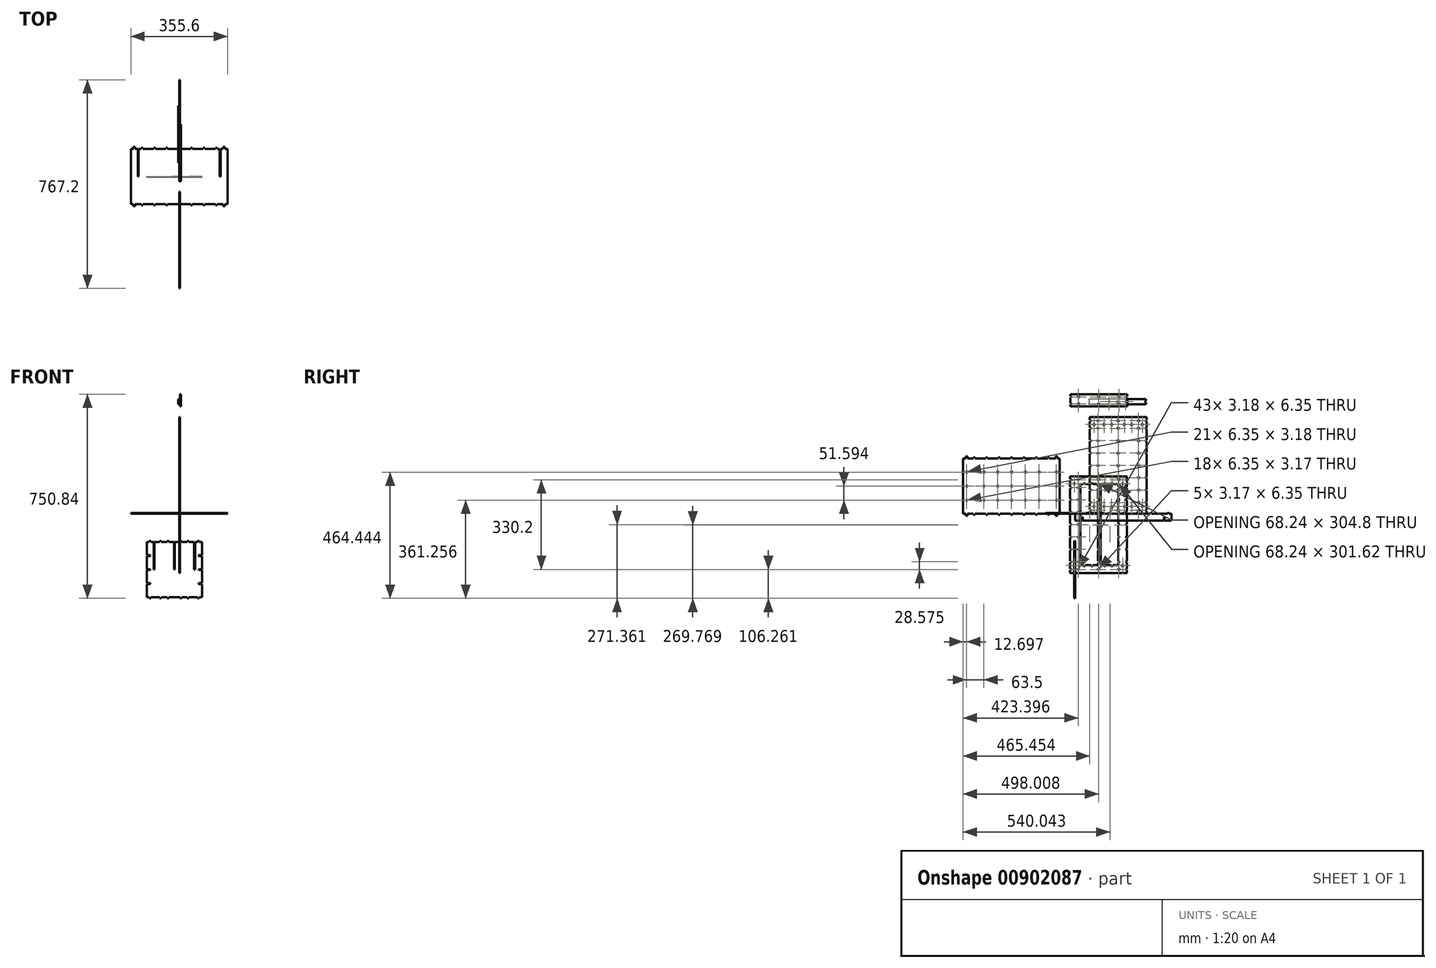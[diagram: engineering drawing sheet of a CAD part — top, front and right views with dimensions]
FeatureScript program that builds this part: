
annotation { "Feature Type Name" : "Feature", "Feature Type Description" : "" }
export const myFeature = defineFeature(function(context is Context, id is Id, definition is map)
    precondition{}
    {
        {
            var Q0;
            Q0=qCreatedBy(makeId("Top.planeOp"),FACE);
            var sketch = newSketch(context, id + "F0", { "sketchPlane" : qUnion([Q0])});
            skLineSegment(sketch, "E0.left", {"start": v(-177.8, 101.6) * mm, "end": v(-177.8, -101.6) * mm});
            skLineSegment(sketch, "E0.right", {"start": v(177.8, 101.6) * mm, "end": v(177.8, -101.6) * mm});
            skPoint(sketch, "E0.middle", {"position": v(0, 0) * mm});
            skLineSegment(sketch, "E1", {"start": v(-152.4, 101.6) * mm, "end": v(-152.4, 0) * mm});
            skLineSegment(sketch, "E2", {"start": v(-149.22, 101.6) * mm, "end": v(-149.22, 0) * mm});
            skLineSegment(sketch, "E3", {"start": v(-152.4, 0) * mm, "end": v(-149.22, 0) * mm});
            skLineSegment(sketch, "E4", {"start": v(149.22, 101.6) * mm, "end": v(149.22, 0) * mm});
            skLineSegment(sketch, "E5", {"start": v(152.4, 101.6) * mm, "end": v(152.4, 0) * mm});
            skLineSegment(sketch, "E6", {"start": v(152.4, 0) * mm, "end": v(149.22, 0) * mm});
            skLineSegment(sketch, "E7", {"start": v(177.8, 101.6) * mm, "end": v(168.28, 101.6) * mm});
            skLineSegment(sketch, "E8", {"start": v(168.28, 101.6) * mm, "end": v(168.28, 105.57) * mm});
            skLineSegment(sketch, "E9", {"start": v(161.93, 105.57) * mm, "end": v(161.93, 101.6) * mm});
            skLineSegment(sketch, "E10", {"start": v(161.93, 101.6) * mm, "end": v(152.4, 101.6) * mm});
            skLineSegment(sketch, "E11", {"start": v(-152.4, 101.6) * mm, "end": v(-161.92, 101.6) * mm});
            skLineSegment(sketch, "E12", {"start": v(-161.92, 101.6) * mm, "end": v(-161.92, 105.57) * mm});
            skLineSegment(sketch, "E13", {"start": v(-168.27, 105.57) * mm, "end": v(-168.27, 101.6) * mm});
            skLineSegment(sketch, "E14", {"start": v(-168.27, 101.6) * mm, "end": v(-177.8, 101.6) * mm});
            skLineSegment(sketch, "E15", {"start": v(-133.35, 101.6) * mm, "end": v(-133.35, 105.57) * mm});
            skLineSegment(sketch, "E16", {"start": v(-133.35, 105.57) * mm, "end": v(-139.7, 105.57) * mm});
            skLineSegment(sketch, "E17", {"start": v(-139.7, 105.57) * mm, "end": v(-139.7, 101.6) * mm});
            skLineSegment(sketch, "E18", {"start": v(48.68, 101.6) * mm, "end": v(48.68, 105.57) * mm});
            skLineSegment(sketch, "E19", {"start": v(48.68, 105.57) * mm, "end": v(42.33, 105.57) * mm});
            skLineSegment(sketch, "E20", {"start": v(42.33, 105.57) * mm, "end": v(42.33, 101.6) * mm});
            skLineSegment(sketch, "E21", {"start": v(-42.33, 101.6) * mm, "end": v(-42.33, 105.57) * mm});
            skLineSegment(sketch, "E22", {"start": v(-42.33, 105.57) * mm, "end": v(-48.68, 105.57) * mm});
            skLineSegment(sketch, "E23", {"start": v(-48.68, 105.57) * mm, "end": v(-48.68, 101.6) * mm});
            skLineSegment(sketch, "E24", {"start": v(3.18, 101.6) * mm, "end": v(3.18, 105.57) * mm});
            skLineSegment(sketch, "E25", {"start": v(3.18, 105.57) * mm, "end": v(-3.17, 105.57) * mm});
            skLineSegment(sketch, "E26", {"start": v(-3.17, 105.57) * mm, "end": v(-3.17, 101.6) * mm});
            skLineSegment(sketch, "E27", {"start": v(139.7, 101.6) * mm, "end": v(139.7, 105.57) * mm});
            skLineSegment(sketch, "E28", {"start": v(139.7, 105.57) * mm, "end": v(133.35, 105.57) * mm});
            skLineSegment(sketch, "E29", {"start": v(133.35, 105.57) * mm, "end": v(133.35, 101.6) * mm});
            skLineSegment(sketch, "E30", {"start": v(149.22, 101.6) * mm, "end": v(139.7, 101.6) * mm});
            skLineSegment(sketch, "E31", {"start": v(42.33, 101.6) * mm, "end": v(3.18, 101.6) * mm});
            skLineSegment(sketch, "E32", {"start": v(-3.17, 101.6) * mm, "end": v(-42.33, 101.6) * mm});
            skLineSegment(sketch, "E33", {"start": v(-139.7, 101.6) * mm, "end": v(-149.22, 101.6) * mm});
            skLineSegment(sketch, "E34", {"start": v(94.2, 101.6) * mm, "end": v(94.2, 105.57) * mm});
            skLineSegment(sketch, "E35", {"start": v(94.2, 105.57) * mm, "end": v(87.84, 105.57) * mm});
            skLineSegment(sketch, "E36", {"start": v(87.84, 105.57) * mm, "end": v(87.84, 101.6) * mm});
            skLineSegment(sketch, "E37", {"start": v(-87.84, 101.6) * mm, "end": v(-87.84, 105.57) * mm});
            skLineSegment(sketch, "E38", {"start": v(-87.84, 105.57) * mm, "end": v(-94.2, 105.57) * mm});
            skLineSegment(sketch, "E39", {"start": v(-94.2, 105.57) * mm, "end": v(-94.2, 101.6) * mm});
            skLineSegment(sketch, "E40", {"start": v(-48.68, 101.6) * mm, "end": v(-87.84, 101.6) * mm});
            skLineSegment(sketch, "E41", {"start": v(-94.2, 101.6) * mm, "end": v(-133.35, 101.6) * mm});
            skLineSegment(sketch, "E42", {"start": v(133.35, 101.6) * mm, "end": v(94.2, 101.6) * mm});
            skLineSegment(sketch, "E43", {"start": v(87.84, 101.6) * mm, "end": v(48.68, 101.6) * mm});
            skLineSegment(sketch, "E44", {"start": v(-177.8, -101.6) * mm, "end": v(-168.27, -101.6) * mm});
            skLineSegment(sketch, "E45", {"start": v(-168.27, -101.6) * mm, "end": v(-168.27, -105.57) * mm});
            skLineSegment(sketch, "E46", {"start": v(-161.92, -105.57) * mm, "end": v(-161.92, -101.6) * mm});
            skLineSegment(sketch, "E47", {"start": v(-161.92, -101.6) * mm, "end": v(-152.4, -101.6) * mm});
            skLineSegment(sketch, "E48", {"start": v(152.4, -101.6) * mm, "end": v(161.93, -101.6) * mm});
            skLineSegment(sketch, "E49", {"start": v(161.93, -101.6) * mm, "end": v(161.93, -105.57) * mm});
            skLineSegment(sketch, "E50", {"start": v(168.28, -105.57) * mm, "end": v(168.28, -101.6) * mm});
            skLineSegment(sketch, "E51", {"start": v(168.28, -101.6) * mm, "end": v(177.8, -101.6) * mm});
            skLineSegment(sketch, "E52", {"start": v(133.35, -101.6) * mm, "end": v(133.35, -105.57) * mm});
            skLineSegment(sketch, "E53", {"start": v(133.35, -105.57) * mm, "end": v(139.7, -105.57) * mm});
            skLineSegment(sketch, "E54", {"start": v(139.7, -105.57) * mm, "end": v(139.7, -101.6) * mm});
            skLineSegment(sketch, "E55", {"start": v(-48.68, -101.6) * mm, "end": v(-48.68, -105.57) * mm});
            skLineSegment(sketch, "E56", {"start": v(-48.68, -105.57) * mm, "end": v(-42.33, -105.57) * mm});
            skLineSegment(sketch, "E57", {"start": v(-42.33, -105.57) * mm, "end": v(-42.33, -101.6) * mm});
            skLineSegment(sketch, "E58", {"start": v(42.33, -101.6) * mm, "end": v(42.33, -105.57) * mm});
            skLineSegment(sketch, "E59", {"start": v(42.33, -105.57) * mm, "end": v(48.68, -105.57) * mm});
            skLineSegment(sketch, "E60", {"start": v(48.68, -105.57) * mm, "end": v(48.68, -101.6) * mm});
            skLineSegment(sketch, "E61", {"start": v(-3.17, -101.6) * mm, "end": v(-3.17, -105.57) * mm});
            skLineSegment(sketch, "E62", {"start": v(-3.17, -105.57) * mm, "end": v(3.18, -105.57) * mm});
            skLineSegment(sketch, "E63", {"start": v(3.18, -105.57) * mm, "end": v(3.18, -101.6) * mm});
            skLineSegment(sketch, "E64", {"start": v(-139.7, -101.6) * mm, "end": v(-139.7, -105.57) * mm});
            skLineSegment(sketch, "E65", {"start": v(-139.7, -105.57) * mm, "end": v(-133.35, -105.57) * mm});
            skLineSegment(sketch, "E66", {"start": v(-133.35, -105.57) * mm, "end": v(-133.35, -101.6) * mm});
            skLineSegment(sketch, "E67", {"start": v(-149.22, -101.6) * mm, "end": v(-139.7, -101.6) * mm});
            skLineSegment(sketch, "E68", {"start": v(-42.33, -101.6) * mm, "end": v(-3.17, -101.6) * mm});
            skLineSegment(sketch, "E69", {"start": v(3.18, -101.6) * mm, "end": v(42.33, -101.6) * mm});
            skLineSegment(sketch, "E70", {"start": v(139.7, -101.6) * mm, "end": v(149.23, -101.6) * mm});
            skLineSegment(sketch, "E71", {"start": v(-94.2, -101.6) * mm, "end": v(-94.2, -105.57) * mm});
            skLineSegment(sketch, "E72", {"start": v(-94.2, -105.57) * mm, "end": v(-87.84, -105.57) * mm});
            skLineSegment(sketch, "E73", {"start": v(-87.84, -105.57) * mm, "end": v(-87.84, -101.6) * mm});
            skLineSegment(sketch, "E74", {"start": v(87.84, -101.6) * mm, "end": v(87.84, -105.57) * mm});
            skLineSegment(sketch, "E75", {"start": v(87.84, -105.57) * mm, "end": v(94.2, -105.57) * mm});
            skLineSegment(sketch, "E76", {"start": v(94.2, -105.57) * mm, "end": v(94.2, -101.6) * mm});
            skLineSegment(sketch, "E77", {"start": v(48.68, -101.6) * mm, "end": v(87.84, -101.6) * mm});
            skLineSegment(sketch, "E78", {"start": v(94.2, -101.6) * mm, "end": v(133.35, -101.6) * mm});
            skLineSegment(sketch, "E79", {"start": v(-133.35, -101.6) * mm, "end": v(-94.2, -101.6) * mm});
            skLineSegment(sketch, "E80", {"start": v(-87.84, -101.6) * mm, "end": v(-48.68, -101.6) * mm});
            skLineSegment(sketch, "E81", {"start": v(152.4, -101.6) * mm, "end": v(149.23, -101.6) * mm});
            skLineSegment(sketch, "E82", {"start": v(-152.4, -101.6) * mm, "end": v(-149.22, -101.6) * mm});
            skLineSegment(sketch, "E83", {"start": v(168.27, 108.87) * mm, "end": v(161.92, 108.87) * mm});
            skLineSegment(sketch, "E84", {"start": v(168.27, 108.87) * mm, "end": v(168.28, 105.57) * mm});
            skLineSegment(sketch, "E85", {"start": v(161.92, 108.87) * mm, "end": v(161.92, 105.57) * mm});
            skLineSegment(sketch, "E86", {"start": v(-161.92, 108.87) * mm, "end": v(-168.27, 108.87) * mm});
            skLineSegment(sketch, "E87", {"start": v(-168.27, 108.87) * mm, "end": v(-168.27, 105.57) * mm});
            skLineSegment(sketch, "E88", {"start": v(-161.92, 105.57) * mm, "end": v(-161.92, 108.87) * mm});
            skLineSegment(sketch, "E89", {"start": v(-168.27, -108.87) * mm, "end": v(-161.92, -108.87) * mm});
            skLineSegment(sketch, "E90", {"start": v(-168.27, -105.57) * mm, "end": v(-168.27, -108.87) * mm});
            skLineSegment(sketch, "E91", {"start": v(-161.92, -105.57) * mm, "end": v(-161.92, -108.87) * mm});
            skLineSegment(sketch, "E92", {"start": v(161.93, -108.87) * mm, "end": v(168.28, -108.87) * mm});
            skLineSegment(sketch, "E93", {"start": v(161.93, -105.57) * mm, "end": v(161.93, -108.87) * mm});
            skLineSegment(sketch, "E94", {"start": v(168.28, -105.57) * mm, "end": v(168.28, -108.87) * mm});
            skSolve(sketch);
        }
        {
            var Q0;
            Q0=makeQuery(id+"F0.imprint","IMPRINT",FACE,{"disambiguationData":[TD([[makeQuery(id+"F0.imprint","IMPRINT",EDGE,{"derivedFrom":sQuery(id+"F0.wireOp",EDGE,"E0.left")}),1.0]])]});
            extrude(context, id + "F1", {"entities" : qUnion([Q0]), "depth" : 3.17 * mm, "offsetDistance" : 25.4 * mm});
        }
        {
            var Q0;
            Q0=qCreatedBy(makeId("Front.planeOp"),FACE);
            var sketch = newSketch(context, id + "F2", { "sketchPlane" : qUnion([Q0])});
            skPoint(sketch, "E95.middle", {"position": v(-17.67, -205.68) * mm});
            skLineSegment(sketch, "E96", {"start": v(-93.87, -104.08) * mm, "end": v(-93.87, -205.68) * mm});
            skLineSegment(sketch, "E97", {"start": v(-90.7, -104.08) * mm, "end": v(-90.7, -205.68) * mm});
            skLineSegment(sketch, "E98", {"start": v(-93.87, -205.68) * mm, "end": v(-90.7, -205.68) * mm});
            skLineSegment(sketch, "E99", {"start": v(55.36, -104.08) * mm, "end": v(55.36, -205.68) * mm});
            skLineSegment(sketch, "E100", {"start": v(58.53, -104.08) * mm, "end": v(58.53, -205.68) * mm});
            skLineSegment(sketch, "E101", {"start": v(58.53, -205.68) * mm, "end": v(55.36, -205.68) * mm});
            skLineSegment(sketch, "E102", {"start": v(-19.25, -205.68) * mm, "end": v(-16.08, -205.68) * mm});
            skLineSegment(sketch, "E103", {"start": v(-119.27, -152.5) * mm, "end": v(-106.57, -152.5) * mm});
            skLineSegment(sketch, "E104", {"start": v(-106.57, -152.5) * mm, "end": v(-106.57, -155.67) * mm});
            skLineSegment(sketch, "E105", {"start": v(-106.57, -155.67) * mm, "end": v(-119.27, -155.67) * mm});
            skLineSegment(sketch, "E106", {"start": v(-119.27, -255.69) * mm, "end": v(-106.57, -255.69) * mm});
            skLineSegment(sketch, "E107", {"start": v(-106.57, -255.69) * mm, "end": v(-106.57, -258.86) * mm});
            skLineSegment(sketch, "E108", {"start": v(-106.57, -258.86) * mm, "end": v(-119.27, -258.86) * mm});
            skLineSegment(sketch, "E109.right", {"start": v(-44.65, -104.08) * mm, "end": v(-44.65, -100.11) * mm});
            skLineSegment(sketch, "E110.bottom", {"start": v(-44.65, -100.11) * mm, "end": v(-38.3, -100.11) * mm});
            skLineSegment(sketch, "E111.right", {"start": v(-38.3, -104.08) * mm, "end": v(-38.3, -100.11) * mm});
            skLineSegment(sketch, "E112.right", {"start": v(-71.64, -104.08) * mm, "end": v(-71.64, -100.11) * mm});
            skLineSegment(sketch, "E113.bottom", {"start": v(-71.64, -100.11) * mm, "end": v(-65.3, -100.11) * mm});
            skLineSegment(sketch, "E114.right", {"start": v(-65.3, -104.08) * mm, "end": v(-65.3, -100.11) * mm});
            skLineSegment(sketch, "E115", {"start": v(-90.7, -104.08) * mm, "end": v(-71.64, -104.08) * mm});
            skLineSegment(sketch, "E116", {"start": v(-65.3, -104.08) * mm, "end": v(-44.65, -104.08) * mm});
            skLineSegment(sketch, "E117", {"start": v(-38.3, -104.08) * mm, "end": v(-19.25, -104.08) * mm});
            skLineSegment(sketch, "E118", {"start": v(-119.27, -104.08) * mm, "end": v(-119.27, -152.5) * mm});
            skLineSegment(sketch, "E119", {"start": v(-119.27, -258.86) * mm, "end": v(-119.27, -307.28) * mm});
            skLineSegment(sketch, "E120", {"start": v(-119.27, -204.1) * mm, "end": v(-106.57, -204.1) * mm});
            skLineSegment(sketch, "E121", {"start": v(-106.57, -204.1) * mm, "end": v(-106.57, -207.27) * mm});
            skLineSegment(sketch, "E122", {"start": v(-106.57, -207.27) * mm, "end": v(-119.27, -207.27) * mm});
            skLineSegment(sketch, "E123", {"start": v(-119.27, -255.69) * mm, "end": v(-119.27, -207.27) * mm});
            skLineSegment(sketch, "E124", {"start": v(-119.27, -204.1) * mm, "end": v(-119.27, -155.67) * mm});
            skLineSegment(sketch, "E125", {"start": v(71.23, -259.78) * mm, "end": v(71.23, -256.6) * mm});
            skLineSegment(sketch, "E126.right", {"start": v(29.96, -104.08) * mm, "end": v(29.96, -100.11) * mm});
            skLineSegment(sketch, "E127.bottom", {"start": v(29.96, -100.11) * mm, "end": v(36.3, -100.11) * mm});
            skLineSegment(sketch, "E128.right", {"start": v(36.3, -104.08) * mm, "end": v(36.3, -100.11) * mm});
            skLineSegment(sketch, "E129.right", {"start": v(2.97, -104.08) * mm, "end": v(2.97, -100.11) * mm});
            skLineSegment(sketch, "E130.bottom", {"start": v(2.97, -100.11) * mm, "end": v(9.32, -100.11) * mm});
            skLineSegment(sketch, "E131.right", {"start": v(9.32, -104.08) * mm, "end": v(9.32, -100.11) * mm});
            skLineSegment(sketch, "E132", {"start": v(-16.08, -104.08) * mm, "end": v(2.97, -104.08) * mm});
            skLineSegment(sketch, "E133", {"start": v(9.32, -104.08) * mm, "end": v(29.96, -104.08) * mm});
            skLineSegment(sketch, "E134", {"start": v(36.3, -104.08) * mm, "end": v(55.36, -104.08) * mm});
            skLineSegment(sketch, "E135.left", {"start": v(74.4, -307.28) * mm, "end": v(74.4, -311.25) * mm});
            skLineSegment(sketch, "E136.right", {"start": v(68.06, -307.28) * mm, "end": v(68.06, -311.25) * mm});
            skLineSegment(sketch, "E137", {"start": v(68.06, -307.28) * mm, "end": v(58.53, -307.28) * mm});
            skLineSegment(sketch, "E138.right", {"start": v(9.32, -307.28) * mm, "end": v(9.32, -311.25) * mm});
            skLineSegment(sketch, "E139.bottom", {"start": v(9.32, -311.25) * mm, "end": v(2.97, -311.25) * mm});
            skLineSegment(sketch, "E140.right", {"start": v(2.97, -307.28) * mm, "end": v(2.97, -311.25) * mm});
            skLineSegment(sketch, "E141.right", {"start": v(36.3, -307.28) * mm, "end": v(36.3, -311.25) * mm});
            skLineSegment(sketch, "E142.bottom", {"start": v(36.3, -311.25) * mm, "end": v(29.96, -311.25) * mm});
            skLineSegment(sketch, "E143.right", {"start": v(29.96, -307.28) * mm, "end": v(29.96, -311.25) * mm});
            skLineSegment(sketch, "E144", {"start": v(55.36, -307.28) * mm, "end": v(36.3, -307.28) * mm});
            skLineSegment(sketch, "E145", {"start": v(29.96, -307.28) * mm, "end": v(9.32, -307.28) * mm});
            skLineSegment(sketch, "E146", {"start": v(2.97, -307.28) * mm, "end": v(-16.08, -307.28) * mm});
            skLineSegment(sketch, "E147.right", {"start": v(-65.3, -307.28) * mm, "end": v(-65.3, -311.25) * mm});
            skLineSegment(sketch, "E148.bottom", {"start": v(-65.3, -311.25) * mm, "end": v(-71.64, -311.25) * mm});
            skLineSegment(sketch, "E149.right", {"start": v(-71.64, -307.28) * mm, "end": v(-71.64, -311.25) * mm});
            skLineSegment(sketch, "E150.right", {"start": v(-38.3, -307.28) * mm, "end": v(-38.3, -311.25) * mm});
            skLineSegment(sketch, "E151.bottom", {"start": v(-38.3, -311.25) * mm, "end": v(-44.65, -311.25) * mm});
            skLineSegment(sketch, "E152.right", {"start": v(-44.65, -307.28) * mm, "end": v(-44.65, -311.25) * mm});
            skLineSegment(sketch, "E153", {"start": v(-19.25, -307.28) * mm, "end": v(-38.3, -307.28) * mm});
            skLineSegment(sketch, "E154", {"start": v(-44.65, -307.28) * mm, "end": v(-65.3, -307.28) * mm});
            skLineSegment(sketch, "E155", {"start": v(-71.64, -307.28) * mm, "end": v(-90.7, -307.28) * mm});
            skLineSegment(sketch, "E156", {"start": v(-93.87, -307.28) * mm, "end": v(-90.7, -307.28) * mm});
            skLineSegment(sketch, "E157", {"start": v(-19.25, -307.28) * mm, "end": v(-16.08, -307.28) * mm});
            skLineSegment(sketch, "E158", {"start": v(55.36, -307.28) * mm, "end": v(58.53, -307.28) * mm});
            skLineSegment(sketch, "E159", {"start": v(83.93, -258.86) * mm, "end": v(71.23, -258.86) * mm});
            skLineSegment(sketch, "E160", {"start": v(71.23, -258.86) * mm, "end": v(71.23, -255.69) * mm});
            skLineSegment(sketch, "E161", {"start": v(71.23, -255.69) * mm, "end": v(83.93, -255.69) * mm});
            skLineSegment(sketch, "E162", {"start": v(83.93, -155.67) * mm, "end": v(71.23, -155.67) * mm});
            skLineSegment(sketch, "E163", {"start": v(71.23, -155.67) * mm, "end": v(71.23, -152.5) * mm});
            skLineSegment(sketch, "E164", {"start": v(71.23, -152.5) * mm, "end": v(83.93, -152.5) * mm});
            skLineSegment(sketch, "E165", {"start": v(83.93, -307.28) * mm, "end": v(83.93, -258.86) * mm});
            skLineSegment(sketch, "E166", {"start": v(83.93, -152.5) * mm, "end": v(83.93, -104.08) * mm});
            skLineSegment(sketch, "E167", {"start": v(83.93, -207.27) * mm, "end": v(71.23, -207.27) * mm});
            skLineSegment(sketch, "E168", {"start": v(71.23, -207.27) * mm, "end": v(71.23, -204.1) * mm});
            skLineSegment(sketch, "E169", {"start": v(71.23, -204.1) * mm, "end": v(83.93, -204.1) * mm});
            skLineSegment(sketch, "E170", {"start": v(83.93, -155.67) * mm, "end": v(83.93, -204.1) * mm});
            skLineSegment(sketch, "E171", {"start": v(83.93, -207.27) * mm, "end": v(83.93, -255.69) * mm});
            skLineSegment(sketch, "E172", {"start": v(74.4, -311.25) * mm, "end": v(68.06, -311.25) * mm});
            skLineSegment(sketch, "E173", {"start": v(83.93, -307.28) * mm, "end": v(74.4, -307.28) * mm});
            skLineSegment(sketch, "E174.left", {"start": v(-103.4, -307.28) * mm, "end": v(-103.4, -311.25) * mm});
            skLineSegment(sketch, "E175.right", {"start": v(-109.74, -307.28) * mm, "end": v(-109.74, -311.25) * mm});
            skLineSegment(sketch, "E176", {"start": v(-109.74, -307.28) * mm, "end": v(-119.27, -307.28) * mm});
            skLineSegment(sketch, "E177", {"start": v(-103.4, -311.25) * mm, "end": v(-109.74, -311.25) * mm});
            skLineSegment(sketch, "E178", {"start": v(-93.87, -307.28) * mm, "end": v(-103.4, -307.28) * mm});
            skLineSegment(sketch, "E179.left", {"start": v(-109.74, -104.08) * mm, "end": v(-109.74, -100.11) * mm});
            skLineSegment(sketch, "E180.right", {"start": v(-103.4, -104.08) * mm, "end": v(-103.4, -100.11) * mm});
            skLineSegment(sketch, "E181", {"start": v(-103.4, -104.08) * mm, "end": v(-93.87, -104.08) * mm});
            skLineSegment(sketch, "E182", {"start": v(-109.74, -100.11) * mm, "end": v(-103.4, -100.11) * mm});
            skLineSegment(sketch, "E183", {"start": v(-119.27, -104.08) * mm, "end": v(-109.74, -104.08) * mm});
            skLineSegment(sketch, "E184.left", {"start": v(68.06, -104.08) * mm, "end": v(68.06, -100.11) * mm});
            skLineSegment(sketch, "E185.right", {"start": v(74.4, -104.08) * mm, "end": v(74.4, -100.11) * mm});
            skLineSegment(sketch, "E186", {"start": v(74.4, -104.08) * mm, "end": v(83.93, -104.08) * mm});
            skLineSegment(sketch, "E187", {"start": v(68.06, -100.11) * mm, "end": v(74.4, -100.11) * mm});
            skLineSegment(sketch, "E188", {"start": v(58.53, -104.08) * mm, "end": v(68.06, -104.08) * mm});
            skLineSegment(sketch, "E189", {"start": v(-19.25, -205.68) * mm, "end": v(-19.25, -104.08) * mm});
            skLineSegment(sketch, "E190", {"start": v(-16.08, -104.08) * mm, "end": v(-16.08, -205.68) * mm});
            skSolve(sketch);
        }
        {
            var Q0;
            Q0=makeQuery(id+"F2.imprint","IMPRINT",FACE,{"disambiguationData":[TD([[makeQuery(id+"F2.imprint","IMPRINT",EDGE,{"derivedFrom":sQuery(id+"F2.wireOp",EDGE,"E96")}),-1.0]])]});
            extrude(context, id + "F3", {"entities" : qUnion([Q0]), "depth" : 3.17 * mm, "offsetDistance" : 25.4 * mm});
        }
        {
            var Q0;
            Q0=qCreatedBy(makeId("Right.planeOp"),FACE);
            var sketch = newSketch(context, id + "F4", { "sketchPlane" : qUnion([Q0])});
            skLineSegment(sketch, "E191.left", {"start": v(0, 0) * mm, "end": v(0, -25.4) * mm});
            skLineSegment(sketch, "E191.right", {"start": v(355.6, 0) * mm, "end": v(355.6, -25.4) * mm});
            skLineSegment(sketch, "E192", {"start": v(28.57, -25.4) * mm, "end": v(28.57, -12.47) * mm});
            skLineSegment(sketch, "E193", {"start": v(25.4, -12.47) * mm, "end": v(28.57, -12.47) * mm});
            skLineSegment(sketch, "E194", {"start": v(25.4, -12.47) * mm, "end": v(25.4, -25.4) * mm});
            skLineSegment(sketch, "E195", {"start": v(330.2, -25.4) * mm, "end": v(330.2, -12.47) * mm});
            skLineSegment(sketch, "E196", {"start": v(327.03, -12.47) * mm, "end": v(330.2, -12.47) * mm});
            skLineSegment(sketch, "E197", {"start": v(327.03, -12.47) * mm, "end": v(327.03, -25.4) * mm});
            skLineSegment(sketch, "E198", {"start": v(355.6, -25.4) * mm, "end": v(330.2, -25.4) * mm});
            skLineSegment(sketch, "E199", {"start": v(327.03, -25.4) * mm, "end": v(28.57, -25.4) * mm});
            skLineSegment(sketch, "E200", {"start": v(25.4, -25.4) * mm, "end": v(0, -25.4) * mm});
            skLineSegment(sketch, "E201.top", {"start": v(9.53, 3.18) * mm, "end": v(15.88, 3.18) * mm});
            skLineSegment(sketch, "E201.left", {"start": v(9.53, 0) * mm, "end": v(9.53, 3.18) * mm});
            skLineSegment(sketch, "E201.right", {"start": v(15.88, 0) * mm, "end": v(15.88, 3.18) * mm});
            skLineSegment(sketch, "E202.top", {"start": v(73.03, 3.18) * mm, "end": v(79.38, 3.18) * mm});
            skLineSegment(sketch, "E202.left", {"start": v(73.03, 0) * mm, "end": v(73.03, 3.18) * mm});
            skLineSegment(sketch, "E202.right", {"start": v(79.38, 0) * mm, "end": v(79.38, 3.18) * mm});
            skLineSegment(sketch, "E203.top", {"start": v(123.83, 3.18) * mm, "end": v(130.18, 3.18) * mm});
            skLineSegment(sketch, "E203.left", {"start": v(123.83, 0) * mm, "end": v(123.83, 3.18) * mm});
            skLineSegment(sketch, "E203.right", {"start": v(130.18, 0) * mm, "end": v(130.18, 3.18) * mm});
            skLineSegment(sketch, "E204.top", {"start": v(174.63, 3.18) * mm, "end": v(180.98, 3.18) * mm});
            skLineSegment(sketch, "E204.left", {"start": v(174.63, 0) * mm, "end": v(174.63, 3.18) * mm});
            skLineSegment(sketch, "E204.right", {"start": v(180.98, 0) * mm, "end": v(180.98, 3.18) * mm});
            skLineSegment(sketch, "E205.top", {"start": v(225.43, 3.18) * mm, "end": v(231.78, 3.18) * mm});
            skLineSegment(sketch, "E205.left", {"start": v(225.43, 0) * mm, "end": v(225.43, 3.18) * mm});
            skLineSegment(sketch, "E205.right", {"start": v(231.78, 0) * mm, "end": v(231.78, 3.18) * mm});
            skLineSegment(sketch, "E206.top", {"start": v(276.23, 3.18) * mm, "end": v(282.58, 3.18) * mm});
            skLineSegment(sketch, "E206.left", {"start": v(276.23, 0) * mm, "end": v(276.23, 3.18) * mm});
            skLineSegment(sketch, "E206.right", {"start": v(282.58, 0) * mm, "end": v(282.58, 3.18) * mm});
            skLineSegment(sketch, "E207.top", {"start": v(339.73, 3.18) * mm, "end": v(346.08, 3.18) * mm});
            skLineSegment(sketch, "E207.left", {"start": v(339.73, 0) * mm, "end": v(339.73, 3.18) * mm});
            skLineSegment(sketch, "E207.right", {"start": v(346.08, 0) * mm, "end": v(346.08, 3.18) * mm});
            skLineSegment(sketch, "E208", {"start": v(355.6, 0) * mm, "end": v(346.08, 0) * mm});
            skLineSegment(sketch, "E209", {"start": v(339.73, 0) * mm, "end": v(282.58, 0) * mm});
            skLineSegment(sketch, "E210", {"start": v(276.23, 0) * mm, "end": v(231.78, 0) * mm});
            skLineSegment(sketch, "E211", {"start": v(225.43, 0) * mm, "end": v(180.98, 0) * mm});
            skLineSegment(sketch, "E212", {"start": v(174.63, 0) * mm, "end": v(130.18, 0) * mm});
            skLineSegment(sketch, "E213", {"start": v(123.83, 0) * mm, "end": v(79.38, 0) * mm});
            skLineSegment(sketch, "E214", {"start": v(73.03, 0) * mm, "end": v(15.88, 0) * mm});
            skLineSegment(sketch, "E215", {"start": v(9.53, 0) * mm, "end": v(0, 0) * mm});
            skSolve(sketch);
        }
        {
            var Q0;
            Q0=makeQuery(id+"F4.imprint","IMPRINT",FACE,{"disambiguationData":[TD([[makeQuery(id+"F4.imprint","IMPRINT",EDGE,{"derivedFrom":sQuery(id+"F4.wireOp",EDGE,"E191.left")}),1.0]])]});
            extrude(context, id + "F5", {"entities" : qUnion([Q0]), "depth" : 3.17 * mm, "offsetDistance" : 25.4 * mm});
        }
        {
            var Q0;
            Q0=qCreatedBy(makeId("Right.planeOp"),FACE);
            var sketch = newSketch(context, id + "F6", { "sketchPlane" : qUnion([Q0])});
            skLineSegment(sketch, "E216.left", {"start": v(-411.6, 203.2) * mm, "end": v(-411.6, 0) * mm});
            skLineSegment(sketch, "E216.right", {"start": v(-56, 203.2) * mm, "end": v(-56, 0) * mm});
            skPoint(sketch, "E216.middle", {"position": v(-233.8, 101.6) * mm});
            skLineSegment(sketch, "E217", {"start": v(-56, 203.2) * mm, "end": v(-65.53, 203.2) * mm});
            skLineSegment(sketch, "E218", {"start": v(-65.53, 203.2) * mm, "end": v(-65.53, 207.17) * mm});
            skLineSegment(sketch, "E219", {"start": v(-71.88, 207.17) * mm, "end": v(-71.88, 203.2) * mm});
            skLineSegment(sketch, "E220", {"start": v(-71.88, 203.2) * mm, "end": v(-81.4, 203.2) * mm});
            skLineSegment(sketch, "E221", {"start": v(-386.2, 203.2) * mm, "end": v(-395.73, 203.2) * mm});
            skLineSegment(sketch, "E222", {"start": v(-395.73, 203.2) * mm, "end": v(-395.73, 207.17) * mm});
            skLineSegment(sketch, "E223", {"start": v(-402.08, 207.17) * mm, "end": v(-402.08, 203.2) * mm});
            skLineSegment(sketch, "E224", {"start": v(-402.08, 203.2) * mm, "end": v(-411.6, 203.2) * mm});
            skLineSegment(sketch, "E225", {"start": v(-367.15, 203.2) * mm, "end": v(-367.15, 207.17) * mm});
            skLineSegment(sketch, "E226", {"start": v(-367.15, 207.17) * mm, "end": v(-373.5, 207.17) * mm});
            skLineSegment(sketch, "E227", {"start": v(-373.5, 207.17) * mm, "end": v(-373.5, 203.2) * mm});
            skLineSegment(sketch, "E228", {"start": v(-185.12, 203.2) * mm, "end": v(-185.12, 207.17) * mm});
            skLineSegment(sketch, "E229", {"start": v(-185.12, 207.17) * mm, "end": v(-191.47, 207.17) * mm});
            skLineSegment(sketch, "E230", {"start": v(-191.47, 207.17) * mm, "end": v(-191.47, 203.2) * mm});
            skLineSegment(sketch, "E231", {"start": v(-276.14, 203.2) * mm, "end": v(-276.14, 207.17) * mm});
            skLineSegment(sketch, "E232", {"start": v(-276.14, 207.17) * mm, "end": v(-282.49, 207.17) * mm});
            skLineSegment(sketch, "E233", {"start": v(-282.49, 207.17) * mm, "end": v(-282.49, 203.2) * mm});
            skLineSegment(sketch, "E234", {"start": v(-230.63, 203.2) * mm, "end": v(-230.63, 207.17) * mm});
            skLineSegment(sketch, "E235", {"start": v(-230.63, 207.17) * mm, "end": v(-236.98, 207.17) * mm});
            skLineSegment(sketch, "E236", {"start": v(-236.98, 207.17) * mm, "end": v(-236.98, 203.2) * mm});
            skLineSegment(sketch, "E237", {"start": v(-94.1, 203.2) * mm, "end": v(-94.1, 207.17) * mm});
            skLineSegment(sketch, "E238", {"start": v(-94.1, 207.17) * mm, "end": v(-100.45, 207.17) * mm});
            skLineSegment(sketch, "E239", {"start": v(-100.45, 207.17) * mm, "end": v(-100.45, 203.2) * mm});
            skLineSegment(sketch, "E240", {"start": v(-84.58, 203.2) * mm, "end": v(-94.1, 203.2) * mm});
            skLineSegment(sketch, "E241", {"start": v(-191.47, 203.2) * mm, "end": v(-230.63, 203.2) * mm});
            skLineSegment(sketch, "E242", {"start": v(-236.98, 203.2) * mm, "end": v(-276.14, 203.2) * mm});
            skLineSegment(sketch, "E243", {"start": v(-373.5, 203.2) * mm, "end": v(-383.03, 203.2) * mm});
            skLineSegment(sketch, "E244", {"start": v(-139.61, 203.2) * mm, "end": v(-139.61, 207.17) * mm});
            skLineSegment(sketch, "E245", {"start": v(-139.61, 207.17) * mm, "end": v(-145.96, 207.17) * mm});
            skLineSegment(sketch, "E246", {"start": v(-145.96, 207.17) * mm, "end": v(-145.96, 203.2) * mm});
            skLineSegment(sketch, "E247", {"start": v(-321.65, 203.2) * mm, "end": v(-321.65, 207.17) * mm});
            skLineSegment(sketch, "E248", {"start": v(-321.65, 207.17) * mm, "end": v(-328, 207.17) * mm});
            skLineSegment(sketch, "E249", {"start": v(-328, 207.17) * mm, "end": v(-328, 203.2) * mm});
            skLineSegment(sketch, "E250", {"start": v(-282.49, 203.2) * mm, "end": v(-321.65, 203.2) * mm});
            skLineSegment(sketch, "E251", {"start": v(-328, 203.2) * mm, "end": v(-367.15, 203.2) * mm});
            skLineSegment(sketch, "E252", {"start": v(-100.45, 203.2) * mm, "end": v(-139.61, 203.2) * mm});
            skLineSegment(sketch, "E253", {"start": v(-145.96, 203.2) * mm, "end": v(-185.12, 203.2) * mm});
            skLineSegment(sketch, "E254", {"start": v(-411.6, 0) * mm, "end": v(-402.08, 0) * mm});
            skLineSegment(sketch, "E255", {"start": v(-402.08, 0) * mm, "end": v(-402.08, -3.97) * mm});
            skLineSegment(sketch, "E256", {"start": v(-395.73, -3.97) * mm, "end": v(-395.73, 0) * mm});
            skLineSegment(sketch, "E257", {"start": v(-395.73, 0) * mm, "end": v(-386.2, 0) * mm});
            skLineSegment(sketch, "E258", {"start": v(-81.4, 0) * mm, "end": v(-71.88, 0) * mm});
            skLineSegment(sketch, "E259", {"start": v(-71.88, 0) * mm, "end": v(-71.88, -3.97) * mm});
            skLineSegment(sketch, "E260", {"start": v(-65.53, -3.97) * mm, "end": v(-65.53, 0) * mm});
            skLineSegment(sketch, "E261", {"start": v(-65.53, 0) * mm, "end": v(-56, 0) * mm});
            skLineSegment(sketch, "E262", {"start": v(-100.45, 0) * mm, "end": v(-100.45, -3.97) * mm});
            skLineSegment(sketch, "E263", {"start": v(-100.45, -3.97) * mm, "end": v(-94.1, -3.97) * mm});
            skLineSegment(sketch, "E264", {"start": v(-94.1, -3.97) * mm, "end": v(-94.1, 0) * mm});
            skLineSegment(sketch, "E265", {"start": v(-282.49, 0) * mm, "end": v(-282.49, -3.97) * mm});
            skLineSegment(sketch, "E266", {"start": v(-282.49, -3.97) * mm, "end": v(-276.14, -3.97) * mm});
            skLineSegment(sketch, "E267", {"start": v(-276.14, -3.97) * mm, "end": v(-276.14, 0) * mm});
            skLineSegment(sketch, "E268", {"start": v(-191.47, 0) * mm, "end": v(-191.47, -3.97) * mm});
            skLineSegment(sketch, "E269", {"start": v(-191.47, -3.97) * mm, "end": v(-185.12, -3.97) * mm});
            skLineSegment(sketch, "E270", {"start": v(-185.12, -3.97) * mm, "end": v(-185.12, 0) * mm});
            skLineSegment(sketch, "E271", {"start": v(-236.98, 0) * mm, "end": v(-236.98, -3.97) * mm});
            skLineSegment(sketch, "E272", {"start": v(-236.98, -3.97) * mm, "end": v(-230.63, -3.97) * mm});
            skLineSegment(sketch, "E273", {"start": v(-230.63, -3.97) * mm, "end": v(-230.63, 0) * mm});
            skLineSegment(sketch, "E274", {"start": v(-373.5, 0) * mm, "end": v(-373.5, -3.97) * mm});
            skLineSegment(sketch, "E275", {"start": v(-373.5, -3.97) * mm, "end": v(-367.15, -3.97) * mm});
            skLineSegment(sketch, "E276", {"start": v(-367.15, -3.97) * mm, "end": v(-367.15, 0) * mm});
            skLineSegment(sketch, "E277", {"start": v(-383.03, 0) * mm, "end": v(-373.5, 0) * mm});
            skLineSegment(sketch, "E278", {"start": v(-276.14, 0) * mm, "end": v(-236.98, 0) * mm});
            skLineSegment(sketch, "E279", {"start": v(-230.63, 0) * mm, "end": v(-191.47, 0) * mm});
            skLineSegment(sketch, "E280", {"start": v(-94.1, 0) * mm, "end": v(-84.58, 0) * mm});
            skLineSegment(sketch, "E281", {"start": v(-328, 0) * mm, "end": v(-328, -3.97) * mm});
            skLineSegment(sketch, "E282", {"start": v(-328, -3.97) * mm, "end": v(-321.65, -3.97) * mm});
            skLineSegment(sketch, "E283", {"start": v(-321.65, -3.97) * mm, "end": v(-321.65, 0) * mm});
            skLineSegment(sketch, "E284", {"start": v(-145.96, 0) * mm, "end": v(-145.96, -3.97) * mm});
            skLineSegment(sketch, "E285", {"start": v(-145.96, -3.97) * mm, "end": v(-139.61, -3.97) * mm});
            skLineSegment(sketch, "E286", {"start": v(-139.61, -3.97) * mm, "end": v(-139.61, 0) * mm});
            skLineSegment(sketch, "E287", {"start": v(-185.12, 0) * mm, "end": v(-145.96, 0) * mm});
            skLineSegment(sketch, "E288", {"start": v(-139.61, 0) * mm, "end": v(-100.45, 0) * mm});
            skLineSegment(sketch, "E289", {"start": v(-367.15, 0) * mm, "end": v(-328, 0) * mm});
            skLineSegment(sketch, "E290", {"start": v(-321.65, 0) * mm, "end": v(-282.49, 0) * mm});
            skLineSegment(sketch, "E291", {"start": v(-81.4, 0) * mm, "end": v(-84.58, 0) * mm});
            skLineSegment(sketch, "E292", {"start": v(-386.2, 0) * mm, "end": v(-383.03, 0) * mm});
            skLineSegment(sketch, "E293", {"start": v(-81.4, 203.2) * mm, "end": v(-84.58, 203.2) * mm});
            skLineSegment(sketch, "E294", {"start": v(-386.2, 203.2) * mm, "end": v(-383.03, 203.2) * mm});
            skLineSegment(sketch, "E295.bottom", {"start": v(-65.53, 154.78) * mm, "end": v(-71.88, 154.78) * mm});
            skLineSegment(sketch, "E295.top", {"start": v(-65.53, 151.6) * mm, "end": v(-71.88, 151.6) * mm});
            skLineSegment(sketch, "E295.left", {"start": v(-65.53, 154.78) * mm, "end": v(-65.53, 151.6) * mm});
            skLineSegment(sketch, "E295.right", {"start": v(-71.88, 154.78) * mm, "end": v(-71.88, 151.6) * mm});
            skLineSegment(sketch, "E296.bottom", {"start": v(-129.03, 154.78) * mm, "end": v(-135.38, 154.78) * mm});
            skLineSegment(sketch, "E296.top", {"start": v(-129.03, 151.6) * mm, "end": v(-135.38, 151.6) * mm});
            skLineSegment(sketch, "E296.left", {"start": v(-129.03, 154.78) * mm, "end": v(-129.03, 151.6) * mm});
            skLineSegment(sketch, "E296.right", {"start": v(-135.38, 154.78) * mm, "end": v(-135.38, 151.6) * mm});
            skLineSegment(sketch, "E297.bottom", {"start": v(-179.83, 154.78) * mm, "end": v(-186.18, 154.78) * mm});
            skLineSegment(sketch, "E297.top", {"start": v(-179.83, 151.6) * mm, "end": v(-186.18, 151.6) * mm});
            skLineSegment(sketch, "E297.left", {"start": v(-179.83, 154.78) * mm, "end": v(-179.83, 151.6) * mm});
            skLineSegment(sketch, "E297.right", {"start": v(-186.18, 154.78) * mm, "end": v(-186.18, 151.6) * mm});
            skLineSegment(sketch, "E298.bottom", {"start": v(-230.63, 154.78) * mm, "end": v(-236.98, 154.78) * mm});
            skLineSegment(sketch, "E298.top", {"start": v(-230.63, 151.6) * mm, "end": v(-236.98, 151.6) * mm});
            skLineSegment(sketch, "E298.left", {"start": v(-230.63, 154.78) * mm, "end": v(-230.63, 151.6) * mm});
            skLineSegment(sketch, "E298.right", {"start": v(-236.98, 154.78) * mm, "end": v(-236.98, 151.6) * mm});
            skLineSegment(sketch, "E299.bottom", {"start": v(-281.43, 154.78) * mm, "end": v(-287.78, 154.78) * mm});
            skLineSegment(sketch, "E299.top", {"start": v(-281.43, 151.6) * mm, "end": v(-287.78, 151.6) * mm});
            skLineSegment(sketch, "E299.left", {"start": v(-281.43, 154.78) * mm, "end": v(-281.43, 151.6) * mm});
            skLineSegment(sketch, "E299.right", {"start": v(-287.78, 154.78) * mm, "end": v(-287.78, 151.6) * mm});
            skLineSegment(sketch, "E300.bottom", {"start": v(-332.23, 154.78) * mm, "end": v(-338.58, 154.78) * mm});
            skLineSegment(sketch, "E300.top", {"start": v(-332.23, 151.6) * mm, "end": v(-338.58, 151.6) * mm});
            skLineSegment(sketch, "E300.left", {"start": v(-332.23, 154.78) * mm, "end": v(-332.23, 151.6) * mm});
            skLineSegment(sketch, "E300.right", {"start": v(-338.58, 154.78) * mm, "end": v(-338.58, 151.6) * mm});
            skLineSegment(sketch, "E301.bottom", {"start": v(-395.73, 154.78) * mm, "end": v(-402.08, 154.78) * mm});
            skLineSegment(sketch, "E301.top", {"start": v(-395.73, 151.6) * mm, "end": v(-402.08, 151.6) * mm});
            skLineSegment(sketch, "E301.left", {"start": v(-395.73, 154.78) * mm, "end": v(-395.73, 151.6) * mm});
            skLineSegment(sketch, "E301.right", {"start": v(-402.08, 154.78) * mm, "end": v(-402.08, 151.6) * mm});
            skLineSegment(sketch, "E302.bottom", {"start": v(-65.53, 103.19) * mm, "end": v(-71.88, 103.19) * mm});
            skLineSegment(sketch, "E302.top", {"start": v(-65.53, 100.01) * mm, "end": v(-71.88, 100.01) * mm});
            skLineSegment(sketch, "E302.left", {"start": v(-65.53, 103.19) * mm, "end": v(-65.53, 100.01) * mm});
            skLineSegment(sketch, "E302.right", {"start": v(-71.88, 103.19) * mm, "end": v(-71.88, 100.01) * mm});
            skLineSegment(sketch, "E303.bottom", {"start": v(-129.03, 103.19) * mm, "end": v(-135.38, 103.19) * mm});
            skLineSegment(sketch, "E303.top", {"start": v(-129.03, 100.01) * mm, "end": v(-135.38, 100.01) * mm});
            skLineSegment(sketch, "E303.left", {"start": v(-129.03, 103.19) * mm, "end": v(-129.03, 100.01) * mm});
            skLineSegment(sketch, "E303.right", {"start": v(-135.38, 103.19) * mm, "end": v(-135.38, 100.01) * mm});
            skLineSegment(sketch, "E304.bottom", {"start": v(-179.83, 103.19) * mm, "end": v(-186.18, 103.19) * mm});
            skLineSegment(sketch, "E304.top", {"start": v(-179.83, 100.01) * mm, "end": v(-186.18, 100.01) * mm});
            skLineSegment(sketch, "E304.left", {"start": v(-179.83, 103.19) * mm, "end": v(-179.83, 100.01) * mm});
            skLineSegment(sketch, "E304.right", {"start": v(-186.18, 103.19) * mm, "end": v(-186.18, 100.01) * mm});
            skLineSegment(sketch, "E305.bottom", {"start": v(-230.63, 103.19) * mm, "end": v(-236.98, 103.19) * mm});
            skLineSegment(sketch, "E305.top", {"start": v(-230.63, 100.01) * mm, "end": v(-236.98, 100.01) * mm});
            skLineSegment(sketch, "E305.left", {"start": v(-230.63, 103.19) * mm, "end": v(-230.63, 100.01) * mm});
            skLineSegment(sketch, "E305.right", {"start": v(-236.98, 103.19) * mm, "end": v(-236.98, 100.01) * mm});
            skLineSegment(sketch, "E306.bottom", {"start": v(-281.43, 103.19) * mm, "end": v(-287.78, 103.19) * mm});
            skLineSegment(sketch, "E306.top", {"start": v(-281.43, 100.01) * mm, "end": v(-287.78, 100.01) * mm});
            skLineSegment(sketch, "E306.left", {"start": v(-281.43, 103.19) * mm, "end": v(-281.43, 100.01) * mm});
            skLineSegment(sketch, "E306.right", {"start": v(-287.78, 103.19) * mm, "end": v(-287.78, 100.01) * mm});
            skLineSegment(sketch, "E307.bottom", {"start": v(-332.23, 103.19) * mm, "end": v(-338.58, 103.19) * mm});
            skLineSegment(sketch, "E307.top", {"start": v(-332.23, 100.01) * mm, "end": v(-338.58, 100.01) * mm});
            skLineSegment(sketch, "E307.left", {"start": v(-332.23, 103.19) * mm, "end": v(-332.23, 100.01) * mm});
            skLineSegment(sketch, "E307.right", {"start": v(-338.58, 103.19) * mm, "end": v(-338.58, 100.01) * mm});
            skLineSegment(sketch, "E308.bottom", {"start": v(-395.73, 103.19) * mm, "end": v(-402.08, 103.19) * mm});
            skLineSegment(sketch, "E308.top", {"start": v(-395.73, 100.01) * mm, "end": v(-402.08, 100.01) * mm});
            skLineSegment(sketch, "E308.left", {"start": v(-395.73, 103.19) * mm, "end": v(-395.73, 100.01) * mm});
            skLineSegment(sketch, "E308.right", {"start": v(-402.08, 103.19) * mm, "end": v(-402.08, 100.01) * mm});
            skLineSegment(sketch, "E309.bottom", {"start": v(-65.53, 51.6) * mm, "end": v(-71.88, 51.6) * mm});
            skLineSegment(sketch, "E309.top", {"start": v(-65.53, 48.42) * mm, "end": v(-71.88, 48.42) * mm});
            skLineSegment(sketch, "E309.left", {"start": v(-65.53, 51.6) * mm, "end": v(-65.53, 48.42) * mm});
            skLineSegment(sketch, "E309.right", {"start": v(-71.88, 51.6) * mm, "end": v(-71.88, 48.42) * mm});
            skLineSegment(sketch, "E310.bottom", {"start": v(-129.03, 51.6) * mm, "end": v(-135.38, 51.6) * mm});
            skLineSegment(sketch, "E310.top", {"start": v(-129.03, 48.42) * mm, "end": v(-135.38, 48.42) * mm});
            skLineSegment(sketch, "E310.left", {"start": v(-129.03, 51.6) * mm, "end": v(-129.03, 48.42) * mm});
            skLineSegment(sketch, "E310.right", {"start": v(-135.38, 51.6) * mm, "end": v(-135.38, 48.42) * mm});
            skLineSegment(sketch, "E311.bottom", {"start": v(-179.83, 51.6) * mm, "end": v(-186.18, 51.6) * mm});
            skLineSegment(sketch, "E311.top", {"start": v(-179.83, 48.42) * mm, "end": v(-186.18, 48.42) * mm});
            skLineSegment(sketch, "E311.left", {"start": v(-179.83, 51.6) * mm, "end": v(-179.83, 48.42) * mm});
            skLineSegment(sketch, "E311.right", {"start": v(-186.18, 51.6) * mm, "end": v(-186.18, 48.42) * mm});
            skLineSegment(sketch, "E312.bottom", {"start": v(-230.63, 51.6) * mm, "end": v(-236.98, 51.6) * mm});
            skLineSegment(sketch, "E312.top", {"start": v(-230.63, 48.42) * mm, "end": v(-236.98, 48.42) * mm});
            skLineSegment(sketch, "E312.left", {"start": v(-230.63, 51.6) * mm, "end": v(-230.63, 48.42) * mm});
            skLineSegment(sketch, "E312.right", {"start": v(-236.98, 51.6) * mm, "end": v(-236.98, 48.42) * mm});
            skLineSegment(sketch, "E313.bottom", {"start": v(-281.43, 51.6) * mm, "end": v(-287.78, 51.6) * mm});
            skLineSegment(sketch, "E313.top", {"start": v(-281.43, 48.42) * mm, "end": v(-287.78, 48.42) * mm});
            skLineSegment(sketch, "E313.left", {"start": v(-281.43, 51.6) * mm, "end": v(-281.43, 48.42) * mm});
            skLineSegment(sketch, "E313.right", {"start": v(-287.78, 51.6) * mm, "end": v(-287.78, 48.42) * mm});
            skLineSegment(sketch, "E314.bottom", {"start": v(-332.23, 51.6) * mm, "end": v(-338.58, 51.6) * mm});
            skLineSegment(sketch, "E314.top", {"start": v(-332.23, 48.42) * mm, "end": v(-338.58, 48.42) * mm});
            skLineSegment(sketch, "E314.left", {"start": v(-332.23, 51.6) * mm, "end": v(-332.23, 48.42) * mm});
            skLineSegment(sketch, "E314.right", {"start": v(-338.58, 51.6) * mm, "end": v(-338.58, 48.42) * mm});
            skLineSegment(sketch, "E315.bottom", {"start": v(-395.73, 51.6) * mm, "end": v(-402.08, 51.6) * mm});
            skLineSegment(sketch, "E315.top", {"start": v(-395.73, 48.42) * mm, "end": v(-402.08, 48.42) * mm});
            skLineSegment(sketch, "E315.left", {"start": v(-395.73, 51.6) * mm, "end": v(-395.73, 48.42) * mm});
            skLineSegment(sketch, "E315.right", {"start": v(-402.08, 51.6) * mm, "end": v(-402.08, 48.42) * mm});
            skLineSegment(sketch, "E316", {"start": v(-395.73, 210.46) * mm, "end": v(-402.08, 210.46) * mm});
            skLineSegment(sketch, "E317", {"start": v(-395.73, 207.17) * mm, "end": v(-395.73, 210.46) * mm});
            skLineSegment(sketch, "E318", {"start": v(-402.08, 207.17) * mm, "end": v(-402.08, 210.46) * mm});
            skLineSegment(sketch, "E319", {"start": v(-65.53, 210.46) * mm, "end": v(-71.88, 210.46) * mm});
            skLineSegment(sketch, "E320", {"start": v(-71.88, 207.17) * mm, "end": v(-71.88, 210.46) * mm});
            skLineSegment(sketch, "E321", {"start": v(-65.53, 210.46) * mm, "end": v(-65.53, 207.17) * mm});
            skLineSegment(sketch, "E322", {"start": v(-71.88, -7.27) * mm, "end": v(-65.53, -7.27) * mm});
            skLineSegment(sketch, "E323", {"start": v(-65.53, -7.27) * mm, "end": v(-65.53, -3.97) * mm});
            skLineSegment(sketch, "E324", {"start": v(-71.88, -7.27) * mm, "end": v(-71.88, -3.97) * mm});
            skLineSegment(sketch, "E325", {"start": v(-402.08, -7.27) * mm, "end": v(-395.73, -7.27) * mm});
            skLineSegment(sketch, "E326", {"start": v(-402.08, -7.27) * mm, "end": v(-402.08, -3.97) * mm});
            skLineSegment(sketch, "E327", {"start": v(-395.73, -3.97) * mm, "end": v(-395.73, -7.27) * mm});
            skSolve(sketch);
        }
        {
            var Q0;
            Q0 = qSketchRegion(id + "F6", true);
            extrude(context, id + "F7", {"entities" : qUnion([Q0]), "depth" : 3.17 * mm, "offsetDistance" : 25.4 * mm});
        }
        {
            var Q0;
            Q0=qCreatedBy(makeId("Right.planeOp"),FACE);
            var sketch = newSketch(context, id + "F8", { "sketchPlane" : qUnion([Q0])});
            skLineSegment(sketch, "E328.bottom", {"start": v(54.04, 0) * mm, "end": v(263.6, 0) * mm});
            skLineSegment(sketch, "E328.top", {"start": v(54.04, 355.6) * mm, "end": v(263.6, 355.6) * mm});
            skLineSegment(sketch, "E329.left", {"start": v(66.74, 25.4) * mm, "end": v(66.74, 28.58) * mm});
            skLineSegment(sketch, "E330.right", {"start": v(131.02, 25.4) * mm, "end": v(131.02, 28.58) * mm});
            skLineSegment(sketch, "E331.bottom", {"start": v(131.02, 28.58) * mm, "end": v(137.37, 28.58) * mm});
            skLineSegment(sketch, "E332.right", {"start": v(137.37, 25.4) * mm, "end": v(137.37, 28.58) * mm});
            skLineSegment(sketch, "E333.right", {"start": v(104.04, 25.4) * mm, "end": v(104.04, 28.58) * mm});
            skLineSegment(sketch, "E334.bottom", {"start": v(104.04, 28.58) * mm, "end": v(110.39, 28.58) * mm});
            skLineSegment(sketch, "E335.right", {"start": v(110.39, 25.4) * mm, "end": v(110.39, 28.58) * mm});
            skLineSegment(sketch, "E336.left", {"start": v(244.54, 25.4) * mm, "end": v(244.54, 28.57) * mm});
            skLineSegment(sketch, "E337.top", {"start": v(244.54, 28.57) * mm, "end": v(250.9, 28.57) * mm});
            skLineSegment(sketch, "E338.right", {"start": v(250.9, 25.4) * mm, "end": v(250.9, 28.57) * mm});
            skLineSegment(sketch, "E339.right", {"start": v(205.64, 25.4) * mm, "end": v(205.64, 28.58) * mm});
            skLineSegment(sketch, "E340.bottom", {"start": v(205.64, 28.58) * mm, "end": v(211.99, 28.58) * mm});
            skLineSegment(sketch, "E341.right", {"start": v(211.99, 25.4) * mm, "end": v(211.99, 28.58) * mm});
            skLineSegment(sketch, "E342.right", {"start": v(178.65, 25.4) * mm, "end": v(178.65, 28.57) * mm});
            skLineSegment(sketch, "E343.bottom", {"start": v(178.65, 28.57) * mm, "end": v(185, 28.57) * mm});
            skLineSegment(sketch, "E344.right", {"start": v(185, 25.4) * mm, "end": v(185, 28.57) * mm});
            skLineSegment(sketch, "E345", {"start": v(250.9, 25.4) * mm, "end": v(244.54, 25.4) * mm});
            skLineSegment(sketch, "E346", {"start": v(211.99, 25.4) * mm, "end": v(205.64, 25.4) * mm});
            skLineSegment(sketch, "E347", {"start": v(185, 25.4) * mm, "end": v(178.65, 25.4) * mm});
            skLineSegment(sketch, "E348", {"start": v(137.37, 25.4) * mm, "end": v(131.02, 25.4) * mm});
            skLineSegment(sketch, "E349", {"start": v(110.39, 25.4) * mm, "end": v(104.04, 25.4) * mm});
            skLineSegment(sketch, "E350", {"start": v(73.1, 25.4) * mm, "end": v(66.74, 25.4) * mm});
            skLineSegment(sketch, "E351", {"start": v(66.74, 28.58) * mm, "end": v(73.1, 28.58) * mm});
            skLineSegment(sketch, "E352", {"start": v(73.1, 28.58) * mm, "end": v(73.1, 25.4) * mm});
            skLineSegment(sketch, "E353.left", {"start": v(66.74, 327.03) * mm, "end": v(66.74, 330.2) * mm});
            skLineSegment(sketch, "E354.right", {"start": v(131.02, 327.02) * mm, "end": v(131.02, 330.2) * mm});
            skLineSegment(sketch, "E355.bottom", {"start": v(131.02, 330.2) * mm, "end": v(137.37, 330.2) * mm});
            skLineSegment(sketch, "E356.right", {"start": v(137.37, 327.02) * mm, "end": v(137.37, 330.2) * mm});
            skLineSegment(sketch, "E357.right", {"start": v(104.04, 327.03) * mm, "end": v(104.04, 330.2) * mm});
            skLineSegment(sketch, "E358.bottom", {"start": v(104.04, 330.2) * mm, "end": v(110.39, 330.2) * mm});
            skLineSegment(sketch, "E359.right", {"start": v(110.39, 327.03) * mm, "end": v(110.39, 330.2) * mm});
            skLineSegment(sketch, "E360.left", {"start": v(244.54, 327.02) * mm, "end": v(244.54, 330.2) * mm});
            skLineSegment(sketch, "E361.top", {"start": v(244.54, 330.2) * mm, "end": v(250.9, 330.2) * mm});
            skLineSegment(sketch, "E362.right", {"start": v(250.9, 327.02) * mm, "end": v(250.9, 330.2) * mm});
            skLineSegment(sketch, "E363.right", {"start": v(205.64, 327.02) * mm, "end": v(205.64, 330.2) * mm});
            skLineSegment(sketch, "E364.bottom", {"start": v(205.64, 330.2) * mm, "end": v(211.99, 330.2) * mm});
            skLineSegment(sketch, "E365.right", {"start": v(211.99, 327.02) * mm, "end": v(211.99, 330.2) * mm});
            skLineSegment(sketch, "E366.right", {"start": v(178.65, 327.02) * mm, "end": v(178.65, 330.2) * mm});
            skLineSegment(sketch, "E367.bottom", {"start": v(178.65, 330.2) * mm, "end": v(185, 330.2) * mm});
            skLineSegment(sketch, "E368.right", {"start": v(185, 327.02) * mm, "end": v(185, 330.2) * mm});
            skLineSegment(sketch, "E369", {"start": v(250.9, 327.02) * mm, "end": v(244.54, 327.02) * mm});
            skLineSegment(sketch, "E370", {"start": v(211.99, 327.03) * mm, "end": v(205.64, 327.03) * mm});
            skLineSegment(sketch, "E371", {"start": v(185, 327.02) * mm, "end": v(178.65, 327.02) * mm});
            skLineSegment(sketch, "E372", {"start": v(137.37, 327.03) * mm, "end": v(131.02, 327.03) * mm});
            skLineSegment(sketch, "E373", {"start": v(110.39, 327.02) * mm, "end": v(104.04, 327.02) * mm});
            skLineSegment(sketch, "E374", {"start": v(73.1, 327.02) * mm, "end": v(66.74, 327.02) * mm});
            skLineSegment(sketch, "E375", {"start": v(66.74, 330.2) * mm, "end": v(73.1, 330.2) * mm});
            skLineSegment(sketch, "E376", {"start": v(73.1, 330.2) * mm, "end": v(73.1, 327.02) * mm});
            skLineSegment(sketch, "E377.left", {"start": v(98.5, 25.4) * mm, "end": v(98.5, 28.58) * mm});
            skLineSegment(sketch, "E378", {"start": v(82.62, 9.53) * mm, "end": v(85.8, 9.53) * mm});
            skLineSegment(sketch, "E379", {"start": v(85.8, 9.53) * mm, "end": v(85.8, 15.88) * mm});
            skLineSegment(sketch, "E380", {"start": v(85.8, 15.87) * mm, "end": v(82.62, 15.87) * mm});
            skLineSegment(sketch, "E381", {"start": v(82.62, 339.72) * mm, "end": v(85.8, 339.72) * mm});
            skLineSegment(sketch, "E382", {"start": v(85.8, 339.72) * mm, "end": v(85.8, 346.07) * mm});
            skLineSegment(sketch, "E383", {"start": v(85.8, 346.07) * mm, "end": v(82.62, 346.07) * mm});
            skLineSegment(sketch, "E384", {"start": v(82.62, 311.15) * mm, "end": v(85.8, 311.15) * mm});
            skLineSegment(sketch, "E385", {"start": v(85.8, 311.15) * mm, "end": v(85.8, 317.5) * mm});
            skLineSegment(sketch, "E386", {"start": v(85.8, 317.5) * mm, "end": v(82.62, 317.5) * mm});
            skLineSegment(sketch, "E387", {"start": v(82.62, 129.12) * mm, "end": v(85.8, 129.12) * mm});
            skLineSegment(sketch, "E388", {"start": v(85.8, 129.12) * mm, "end": v(85.8, 135.47) * mm});
            skLineSegment(sketch, "E389", {"start": v(85.8, 135.47) * mm, "end": v(82.62, 135.47) * mm});
            skLineSegment(sketch, "E390", {"start": v(82.62, 220.13) * mm, "end": v(85.8, 220.13) * mm});
            skLineSegment(sketch, "E391", {"start": v(85.8, 220.13) * mm, "end": v(85.8, 226.48) * mm});
            skLineSegment(sketch, "E392", {"start": v(85.8, 226.48) * mm, "end": v(82.62, 226.48) * mm});
            skLineSegment(sketch, "E393", {"start": v(82.62, 174.62) * mm, "end": v(85.8, 174.62) * mm});
            skLineSegment(sketch, "E394", {"start": v(85.8, 174.62) * mm, "end": v(85.8, 180.97) * mm});
            skLineSegment(sketch, "E395", {"start": v(85.8, 180.97) * mm, "end": v(82.62, 180.97) * mm});
            skLineSegment(sketch, "E396", {"start": v(82.62, 38.1) * mm, "end": v(85.8, 38.1) * mm});
            skLineSegment(sketch, "E397", {"start": v(85.8, 38.1) * mm, "end": v(85.8, 44.45) * mm});
            skLineSegment(sketch, "E398", {"start": v(85.8, 44.45) * mm, "end": v(82.62, 44.45) * mm});
            skLineSegment(sketch, "E399", {"start": v(82.62, 83.6) * mm, "end": v(85.8, 83.6) * mm});
            skLineSegment(sketch, "E400", {"start": v(85.8, 83.6) * mm, "end": v(85.8, 89.96) * mm});
            skLineSegment(sketch, "E401", {"start": v(85.8, 89.96) * mm, "end": v(82.62, 89.96) * mm});
            skLineSegment(sketch, "E402", {"start": v(82.62, 265.64) * mm, "end": v(85.8, 265.64) * mm});
            skLineSegment(sketch, "E403", {"start": v(85.8, 265.64) * mm, "end": v(85.8, 272) * mm});
            skLineSegment(sketch, "E404", {"start": v(85.8, 272) * mm, "end": v(82.62, 272) * mm});
            skLineSegment(sketch, "E405.left", {"start": v(228.67, 330.2) * mm, "end": v(228.67, 327.02) * mm});
            skLineSegment(sketch, "E406", {"start": v(54.04, 9.53) * mm, "end": v(57.22, 9.53) * mm});
            skLineSegment(sketch, "E407", {"start": v(57.22, 9.53) * mm, "end": v(57.22, 15.88) * mm});
            skLineSegment(sketch, "E408", {"start": v(57.22, 15.88) * mm, "end": v(54.04, 15.88) * mm});
            skLineSegment(sketch, "E409", {"start": v(54.04, 15.88) * mm, "end": v(54.04, 25.4) * mm});
            skLineSegment(sketch, "E410", {"start": v(54.04, 330.2) * mm, "end": v(54.04, 339.73) * mm});
            skLineSegment(sketch, "E411", {"start": v(54.04, 339.73) * mm, "end": v(57.22, 339.73) * mm});
            skLineSegment(sketch, "E412", {"start": v(57.22, 339.73) * mm, "end": v(57.22, 346.08) * mm});
            skLineSegment(sketch, "E413", {"start": v(57.22, 346.08) * mm, "end": v(54.04, 346.08) * mm});
            skLineSegment(sketch, "E414", {"start": v(54.04, 311.15) * mm, "end": v(57.22, 311.15) * mm});
            skLineSegment(sketch, "E415", {"start": v(57.22, 311.15) * mm, "end": v(57.22, 317.5) * mm});
            skLineSegment(sketch, "E416", {"start": v(57.22, 317.5) * mm, "end": v(54.04, 317.5) * mm});
            skLineSegment(sketch, "E417", {"start": v(54.04, 129.12) * mm, "end": v(57.22, 129.12) * mm});
            skLineSegment(sketch, "E418", {"start": v(57.22, 129.12) * mm, "end": v(57.22, 135.47) * mm});
            skLineSegment(sketch, "E419", {"start": v(57.22, 135.47) * mm, "end": v(54.04, 135.47) * mm});
            skLineSegment(sketch, "E420", {"start": v(54.04, 220.13) * mm, "end": v(57.22, 220.13) * mm});
            skLineSegment(sketch, "E421", {"start": v(57.22, 220.13) * mm, "end": v(57.22, 226.48) * mm});
            skLineSegment(sketch, "E422", {"start": v(57.22, 226.48) * mm, "end": v(54.04, 226.48) * mm});
            skLineSegment(sketch, "E423", {"start": v(54.04, 174.63) * mm, "end": v(57.22, 174.63) * mm});
            skLineSegment(sketch, "E424", {"start": v(57.22, 174.63) * mm, "end": v(57.22, 180.98) * mm});
            skLineSegment(sketch, "E425", {"start": v(57.22, 180.98) * mm, "end": v(54.04, 180.98) * mm});
            skLineSegment(sketch, "E426", {"start": v(54.04, 38.1) * mm, "end": v(57.22, 38.1) * mm});
            skLineSegment(sketch, "E427", {"start": v(57.22, 38.1) * mm, "end": v(57.22, 44.45) * mm});
            skLineSegment(sketch, "E428", {"start": v(57.22, 44.45) * mm, "end": v(54.04, 44.45) * mm});
            skLineSegment(sketch, "E429", {"start": v(54.04, 28.58) * mm, "end": v(54.04, 38.1) * mm});
            skLineSegment(sketch, "E430", {"start": v(54.04, 135.47) * mm, "end": v(54.04, 174.63) * mm});
            skLineSegment(sketch, "E431", {"start": v(54.04, 180.98) * mm, "end": v(54.04, 220.13) * mm});
            skLineSegment(sketch, "E432", {"start": v(54.04, 317.5) * mm, "end": v(54.04, 327.03) * mm});
            skLineSegment(sketch, "E433", {"start": v(54.04, 83.6) * mm, "end": v(57.22, 83.6) * mm});
            skLineSegment(sketch, "E434", {"start": v(57.22, 83.6) * mm, "end": v(57.22, 89.96) * mm});
            skLineSegment(sketch, "E435", {"start": v(57.22, 89.96) * mm, "end": v(54.04, 89.96) * mm});
            skLineSegment(sketch, "E436", {"start": v(54.04, 265.64) * mm, "end": v(57.22, 265.64) * mm});
            skLineSegment(sketch, "E437", {"start": v(57.22, 265.64) * mm, "end": v(57.22, 272) * mm});
            skLineSegment(sketch, "E438", {"start": v(57.22, 272) * mm, "end": v(54.04, 272) * mm});
            skLineSegment(sketch, "E439", {"start": v(54.04, 226.48) * mm, "end": v(54.04, 265.64) * mm});
            skLineSegment(sketch, "E440", {"start": v(54.04, 272) * mm, "end": v(54.04, 311.15) * mm});
            skLineSegment(sketch, "E441", {"start": v(54.04, 44.45) * mm, "end": v(54.04, 83.6) * mm});
            skLineSegment(sketch, "E442", {"start": v(54.04, 89.96) * mm, "end": v(54.04, 129.12) * mm});
            skLineSegment(sketch, "E443", {"start": v(54.04, 330.2) * mm, "end": v(54.04, 327.03) * mm});
            skLineSegment(sketch, "E444", {"start": v(54.04, 25.4) * mm, "end": v(54.04, 28.58) * mm});
            skLineSegment(sketch, "E445", {"start": v(263.6, 346.07) * mm, "end": v(260.42, 346.07) * mm});
            skLineSegment(sketch, "E446", {"start": v(260.42, 346.07) * mm, "end": v(260.42, 339.72) * mm});
            skLineSegment(sketch, "E447", {"start": v(260.42, 339.72) * mm, "end": v(263.6, 339.72) * mm});
            skLineSegment(sketch, "E448", {"start": v(263.6, 339.72) * mm, "end": v(263.6, 330.2) * mm});
            skLineSegment(sketch, "E449", {"start": v(263.6, 25.4) * mm, "end": v(263.6, 15.87) * mm});
            skLineSegment(sketch, "E450", {"start": v(263.6, 15.87) * mm, "end": v(260.42, 15.87) * mm});
            skLineSegment(sketch, "E451", {"start": v(260.42, 15.87) * mm, "end": v(260.42, 9.52) * mm});
            skLineSegment(sketch, "E452", {"start": v(260.42, 9.52) * mm, "end": v(263.6, 9.52) * mm});
            skLineSegment(sketch, "E453", {"start": v(263.6, 44.45) * mm, "end": v(260.42, 44.45) * mm});
            skLineSegment(sketch, "E454", {"start": v(260.42, 44.45) * mm, "end": v(260.42, 38.1) * mm});
            skLineSegment(sketch, "E455", {"start": v(260.42, 38.1) * mm, "end": v(263.6, 38.1) * mm});
            skLineSegment(sketch, "E456", {"start": v(263.6, 226.48) * mm, "end": v(260.42, 226.48) * mm});
            skLineSegment(sketch, "E457", {"start": v(260.42, 226.48) * mm, "end": v(260.42, 220.13) * mm});
            skLineSegment(sketch, "E458", {"start": v(260.42, 220.13) * mm, "end": v(263.6, 220.13) * mm});
            skLineSegment(sketch, "E459", {"start": v(263.6, 135.47) * mm, "end": v(260.42, 135.47) * mm});
            skLineSegment(sketch, "E460", {"start": v(260.42, 135.47) * mm, "end": v(260.42, 129.12) * mm});
            skLineSegment(sketch, "E461", {"start": v(260.42, 129.12) * mm, "end": v(263.6, 129.12) * mm});
            skLineSegment(sketch, "E462", {"start": v(263.6, 180.97) * mm, "end": v(260.42, 180.97) * mm});
            skLineSegment(sketch, "E463", {"start": v(260.42, 180.97) * mm, "end": v(260.42, 174.62) * mm});
            skLineSegment(sketch, "E464", {"start": v(260.42, 174.62) * mm, "end": v(263.6, 174.62) * mm});
            skLineSegment(sketch, "E465", {"start": v(263.6, 317.5) * mm, "end": v(260.42, 317.5) * mm});
            skLineSegment(sketch, "E466", {"start": v(260.42, 317.5) * mm, "end": v(260.42, 311.15) * mm});
            skLineSegment(sketch, "E467", {"start": v(260.42, 311.15) * mm, "end": v(263.6, 311.15) * mm});
            skLineSegment(sketch, "E468", {"start": v(263.6, 327.02) * mm, "end": v(263.6, 317.5) * mm});
            skLineSegment(sketch, "E469", {"start": v(263.6, 220.13) * mm, "end": v(263.6, 180.97) * mm});
            skLineSegment(sketch, "E470", {"start": v(263.6, 174.62) * mm, "end": v(263.6, 135.47) * mm});
            skLineSegment(sketch, "E471", {"start": v(263.6, 38.1) * mm, "end": v(263.6, 28.57) * mm});
            skLineSegment(sketch, "E472", {"start": v(263.6, 272) * mm, "end": v(260.42, 272) * mm});
            skLineSegment(sketch, "E473", {"start": v(260.42, 272) * mm, "end": v(260.42, 265.64) * mm});
            skLineSegment(sketch, "E474", {"start": v(260.42, 265.64) * mm, "end": v(263.6, 265.64) * mm});
            skLineSegment(sketch, "E475", {"start": v(263.6, 89.96) * mm, "end": v(260.42, 89.96) * mm});
            skLineSegment(sketch, "E476", {"start": v(260.42, 89.96) * mm, "end": v(260.42, 83.6) * mm});
            skLineSegment(sketch, "E477", {"start": v(260.42, 83.6) * mm, "end": v(263.6, 83.6) * mm});
            skLineSegment(sketch, "E478", {"start": v(263.6, 129.12) * mm, "end": v(263.6, 89.96) * mm});
            skLineSegment(sketch, "E479", {"start": v(263.6, 265.64) * mm, "end": v(263.6, 226.48) * mm});
            skLineSegment(sketch, "E480", {"start": v(263.6, 25.4) * mm, "end": v(263.6, 28.57) * mm});
            skLineSegment(sketch, "E481", {"start": v(263.6, 330.2) * mm, "end": v(263.6, 327.02) * mm});
            skLineSegment(sketch, "E482", {"start": v(231.84, 9.52) * mm, "end": v(235.02, 9.52) * mm});
            skLineSegment(sketch, "E483", {"start": v(235.02, 9.52) * mm, "end": v(235.02, 15.87) * mm});
            skLineSegment(sketch, "E484", {"start": v(235.02, 15.87) * mm, "end": v(231.84, 15.87) * mm});
            skLineSegment(sketch, "E485", {"start": v(231.84, 339.72) * mm, "end": v(235.02, 339.72) * mm});
            skLineSegment(sketch, "E486", {"start": v(235.02, 339.72) * mm, "end": v(235.02, 346.07) * mm});
            skLineSegment(sketch, "E487", {"start": v(235.02, 346.07) * mm, "end": v(231.84, 346.07) * mm});
            skLineSegment(sketch, "E488", {"start": v(231.84, 311.15) * mm, "end": v(235.02, 311.15) * mm});
            skLineSegment(sketch, "E489", {"start": v(235.02, 311.15) * mm, "end": v(235.02, 317.5) * mm});
            skLineSegment(sketch, "E490", {"start": v(235.02, 317.5) * mm, "end": v(231.84, 317.5) * mm});
            skLineSegment(sketch, "E491", {"start": v(231.84, 129.12) * mm, "end": v(235.02, 129.12) * mm});
            skLineSegment(sketch, "E492", {"start": v(235.02, 129.12) * mm, "end": v(235.02, 135.47) * mm});
            skLineSegment(sketch, "E493", {"start": v(235.02, 135.47) * mm, "end": v(231.84, 135.47) * mm});
            skLineSegment(sketch, "E494", {"start": v(231.84, 220.13) * mm, "end": v(235.02, 220.13) * mm});
            skLineSegment(sketch, "E495", {"start": v(235.02, 220.13) * mm, "end": v(235.02, 226.48) * mm});
            skLineSegment(sketch, "E496", {"start": v(235.02, 226.48) * mm, "end": v(231.84, 226.48) * mm});
            skLineSegment(sketch, "E497", {"start": v(231.84, 174.62) * mm, "end": v(235.02, 174.62) * mm});
            skLineSegment(sketch, "E498", {"start": v(235.02, 174.62) * mm, "end": v(235.02, 180.97) * mm});
            skLineSegment(sketch, "E499", {"start": v(235.02, 180.97) * mm, "end": v(231.84, 180.97) * mm});
            skLineSegment(sketch, "E500", {"start": v(231.84, 38.1) * mm, "end": v(235.02, 38.1) * mm});
            skLineSegment(sketch, "E501", {"start": v(235.02, 38.1) * mm, "end": v(235.02, 44.45) * mm});
            skLineSegment(sketch, "E502", {"start": v(235.02, 44.45) * mm, "end": v(231.84, 44.45) * mm});
            skLineSegment(sketch, "E503", {"start": v(231.84, 83.6) * mm, "end": v(235.02, 83.6) * mm});
            skLineSegment(sketch, "E504", {"start": v(235.02, 83.6) * mm, "end": v(235.02, 89.96) * mm});
            skLineSegment(sketch, "E505", {"start": v(235.02, 89.96) * mm, "end": v(231.84, 89.96) * mm});
            skLineSegment(sketch, "E506", {"start": v(231.84, 265.64) * mm, "end": v(235.02, 265.64) * mm});
            skLineSegment(sketch, "E507", {"start": v(235.02, 265.64) * mm, "end": v(235.02, 272) * mm});
            skLineSegment(sketch, "E508", {"start": v(235.02, 272) * mm, "end": v(231.84, 272) * mm});
            skLineSegment(sketch, "E509", {"start": v(231.84, 330.2) * mm, "end": v(231.84, 327.02) * mm});
            skLineSegment(sketch, "E510", {"start": v(157.23, 9.52) * mm, "end": v(160.4, 9.52) * mm});
            skLineSegment(sketch, "E511", {"start": v(160.4, 9.52) * mm, "end": v(160.4, 15.87) * mm});
            skLineSegment(sketch, "E512", {"start": v(160.4, 15.87) * mm, "end": v(157.23, 15.87) * mm});
            skLineSegment(sketch, "E513", {"start": v(157.23, 339.72) * mm, "end": v(160.4, 339.72) * mm});
            skLineSegment(sketch, "E514", {"start": v(160.4, 339.72) * mm, "end": v(160.4, 346.07) * mm});
            skLineSegment(sketch, "E515", {"start": v(160.4, 346.07) * mm, "end": v(157.23, 346.07) * mm});
            skLineSegment(sketch, "E516", {"start": v(157.23, 311.15) * mm, "end": v(160.4, 311.15) * mm});
            skLineSegment(sketch, "E517", {"start": v(160.4, 311.15) * mm, "end": v(160.4, 317.5) * mm});
            skLineSegment(sketch, "E518", {"start": v(160.4, 317.5) * mm, "end": v(157.23, 317.5) * mm});
            skLineSegment(sketch, "E519", {"start": v(157.23, 129.12) * mm, "end": v(160.4, 129.12) * mm});
            skLineSegment(sketch, "E520", {"start": v(160.4, 129.12) * mm, "end": v(160.4, 135.47) * mm});
            skLineSegment(sketch, "E521", {"start": v(160.4, 135.47) * mm, "end": v(157.23, 135.47) * mm});
            skLineSegment(sketch, "E522", {"start": v(157.23, 220.13) * mm, "end": v(160.4, 220.13) * mm});
            skLineSegment(sketch, "E523", {"start": v(160.4, 220.13) * mm, "end": v(160.4, 226.48) * mm});
            skLineSegment(sketch, "E524", {"start": v(160.4, 226.48) * mm, "end": v(157.23, 226.48) * mm});
            skLineSegment(sketch, "E525", {"start": v(157.23, 174.62) * mm, "end": v(160.4, 174.62) * mm});
            skLineSegment(sketch, "E526", {"start": v(160.4, 174.62) * mm, "end": v(160.4, 180.97) * mm});
            skLineSegment(sketch, "E527", {"start": v(160.4, 180.97) * mm, "end": v(157.23, 180.97) * mm});
            skLineSegment(sketch, "E528", {"start": v(157.23, 38.1) * mm, "end": v(160.4, 38.1) * mm});
            skLineSegment(sketch, "E529", {"start": v(160.4, 38.1) * mm, "end": v(160.4, 44.45) * mm});
            skLineSegment(sketch, "E530", {"start": v(160.4, 44.45) * mm, "end": v(157.23, 44.45) * mm});
            skLineSegment(sketch, "E531", {"start": v(157.23, 83.6) * mm, "end": v(160.4, 83.6) * mm});
            skLineSegment(sketch, "E532", {"start": v(160.4, 83.6) * mm, "end": v(160.4, 89.96) * mm});
            skLineSegment(sketch, "E533", {"start": v(160.4, 89.96) * mm, "end": v(157.23, 89.96) * mm});
            skLineSegment(sketch, "E534", {"start": v(157.23, 265.64) * mm, "end": v(160.4, 265.64) * mm});
            skLineSegment(sketch, "E535", {"start": v(160.4, 265.64) * mm, "end": v(160.4, 272) * mm});
            skLineSegment(sketch, "E536", {"start": v(160.4, 272) * mm, "end": v(157.23, 272) * mm});
            skLineSegment(sketch, "E537", {"start": v(54.04, 9.53) * mm, "end": v(54.04, 0) * mm});
            skLineSegment(sketch, "E538", {"start": v(54.04, 346.08) * mm, "end": v(54.04, 355.6) * mm});
            skLineSegment(sketch, "E539", {"start": v(82.62, 346.07) * mm, "end": v(82.62, 339.72) * mm});
            skLineSegment(sketch, "E540", {"start": v(82.62, 317.5) * mm, "end": v(82.62, 311.15) * mm});
            skLineSegment(sketch, "E541", {"start": v(82.62, 272) * mm, "end": v(82.62, 265.64) * mm});
            skLineSegment(sketch, "E542", {"start": v(231.84, 9.52) * mm, "end": v(231.84, 15.87) * mm});
            skLineSegment(sketch, "E543", {"start": v(231.84, 38.1) * mm, "end": v(231.84, 44.45) * mm});
            skLineSegment(sketch, "E544", {"start": v(231.84, 83.6) * mm, "end": v(231.84, 89.96) * mm});
            skLineSegment(sketch, "E545", {"start": v(231.84, 129.12) * mm, "end": v(231.84, 135.47) * mm});
            skLineSegment(sketch, "E546", {"start": v(231.84, 174.62) * mm, "end": v(231.84, 180.97) * mm});
            skLineSegment(sketch, "E547", {"start": v(231.84, 220.13) * mm, "end": v(231.84, 226.48) * mm});
            skLineSegment(sketch, "E548", {"start": v(157.23, 226.48) * mm, "end": v(157.23, 220.13) * mm});
            skLineSegment(sketch, "E549", {"start": v(157.23, 180.97) * mm, "end": v(157.23, 174.62) * mm});
            skLineSegment(sketch, "E550", {"start": v(82.62, 226.48) * mm, "end": v(82.62, 220.13) * mm});
            skLineSegment(sketch, "E551", {"start": v(82.62, 180.97) * mm, "end": v(82.62, 174.62) * mm});
            skLineSegment(sketch, "E552", {"start": v(157.23, 346.07) * mm, "end": v(157.23, 339.72) * mm});
            skLineSegment(sketch, "E553", {"start": v(157.23, 317.5) * mm, "end": v(157.23, 311.15) * mm});
            skLineSegment(sketch, "E554", {"start": v(157.23, 272) * mm, "end": v(157.23, 265.64) * mm});
            skLineSegment(sketch, "E555", {"start": v(157.23, 135.47) * mm, "end": v(157.23, 129.12) * mm});
            skLineSegment(sketch, "E556", {"start": v(157.23, 89.96) * mm, "end": v(157.23, 83.6) * mm});
            skLineSegment(sketch, "E557", {"start": v(157.23, 44.45) * mm, "end": v(157.23, 38.1) * mm});
            skLineSegment(sketch, "E558", {"start": v(157.23, 15.87) * mm, "end": v(157.23, 9.52) * mm});
            skLineSegment(sketch, "E559", {"start": v(82.62, 9.53) * mm, "end": v(82.62, 15.87) * mm});
            skLineSegment(sketch, "E560", {"start": v(82.62, 135.47) * mm, "end": v(82.62, 129.12) * mm});
            skLineSegment(sketch, "E561", {"start": v(82.62, 89.96) * mm, "end": v(82.62, 83.6) * mm});
            skLineSegment(sketch, "E562", {"start": v(82.62, 44.45) * mm, "end": v(82.62, 38.1) * mm});
            skLineSegment(sketch, "E563", {"start": v(231.84, 317.5) * mm, "end": v(231.84, 311.15) * mm});
            skLineSegment(sketch, "E564", {"start": v(231.84, 272) * mm, "end": v(231.84, 265.64) * mm});
            skLineSegment(sketch, "E565", {"start": v(263.6, 346.07) * mm, "end": v(263.6, 355.6) * mm});
            skLineSegment(sketch, "E566", {"start": v(263.6, 83.6) * mm, "end": v(263.6, 44.45) * mm});
            skLineSegment(sketch, "E567", {"start": v(263.6, 9.52) * mm, "end": v(263.6, 0) * mm});
            skLineSegment(sketch, "E568", {"start": v(263.6, 311.15) * mm, "end": v(263.6, 272) * mm});
            skLineSegment(sketch, "E569", {"start": v(231.84, 339.72) * mm, "end": v(231.84, 346.07) * mm});
            skSolve(sketch);
        }
        {
            var Q0;
            {var subQ24=sQuery(id+"F8.wireOp",EDGE,"E328.bottom");Q0=makeQuery(id+"F8.imprint","IMPRINT",FACE,{"disambiguationData":[TD([[makeQuery(id+"F8.imprint","IMPRINT",EDGE,{"derivedFrom":subQ24}),1.0]])]});}
            extrude(context, id + "F9", {"entities" : qUnion([Q0]), "depth" : 3.17 * mm, "offsetDistance" : 25.4 * mm});
        }
        {
            var Q0;
            Q0=qCreatedBy(makeId("Right.planeOp"),FACE);
            var sketch = newSketch(context, id + "F10", { "sketchPlane" : qUnion([Q0])});
            skLineSegment(sketch, "E570.bottom", {"start": v(-18.37, -217.69) * mm, "end": v(191.18, -217.69) * mm});
            skLineSegment(sketch, "E570.top", {"start": v(-18.37, 137.91) * mm, "end": v(191.18, 137.91) * mm});
            skLineSegment(sketch, "E571.left", {"start": v(-5.67, -192.29) * mm, "end": v(-5.67, -189.11) * mm});
            skLineSegment(sketch, "E572.right", {"start": v(58.62, -192.29) * mm, "end": v(58.62, -189.11) * mm});
            skLineSegment(sketch, "E573.right", {"start": v(64.97, -192.29) * mm, "end": v(64.97, -189.11) * mm});
            skLineSegment(sketch, "E574.right", {"start": v(31.63, -192.29) * mm, "end": v(31.63, -189.11) * mm});
            skLineSegment(sketch, "E575.right", {"start": v(37.98, -192.29) * mm, "end": v(37.98, -189.11) * mm});
            skLineSegment(sketch, "E576.left", {"start": v(172.13, -192.29) * mm, "end": v(172.13, -189.11) * mm});
            skLineSegment(sketch, "E577.top", {"start": v(172.13, -189.11) * mm, "end": v(178.48, -189.11) * mm});
            skLineSegment(sketch, "E578.right", {"start": v(178.48, -192.29) * mm, "end": v(178.48, -189.11) * mm});
            skLineSegment(sketch, "E579.right", {"start": v(133.23, -192.29) * mm, "end": v(133.23, -189.11) * mm});
            skLineSegment(sketch, "E580.right", {"start": v(139.58, -192.29) * mm, "end": v(139.58, -189.11) * mm});
            skLineSegment(sketch, "E581.right", {"start": v(106.24, -192.29) * mm, "end": v(106.24, -189.11) * mm});
            skLineSegment(sketch, "E582.right", {"start": v(112.6, -192.29) * mm, "end": v(112.6, -189.11) * mm});
            skLineSegment(sketch, "E583", {"start": v(178.48, -192.29) * mm, "end": v(172.13, -192.29) * mm});
            skLineSegment(sketch, "E584", {"start": v(139.58, -192.29) * mm, "end": v(133.23, -192.29) * mm});
            skLineSegment(sketch, "E585", {"start": v(112.6, -192.29) * mm, "end": v(106.24, -192.29) * mm});
            skLineSegment(sketch, "E586", {"start": v(64.97, -192.29) * mm, "end": v(58.62, -192.29) * mm});
            skLineSegment(sketch, "E587", {"start": v(37.98, -192.29) * mm, "end": v(31.63, -192.29) * mm});
            skLineSegment(sketch, "E588", {"start": v(0.68, -192.29) * mm, "end": v(-5.67, -192.29) * mm});
            skLineSegment(sketch, "E589", {"start": v(-5.67, -189.11) * mm, "end": v(0.68, -189.11) * mm});
            skLineSegment(sketch, "E590", {"start": v(0.68, -189.11) * mm, "end": v(0.68, -192.29) * mm});
            skLineSegment(sketch, "E591.left", {"start": v(-5.67, 109.34) * mm, "end": v(-5.67, 112.51) * mm});
            skLineSegment(sketch, "E592.right", {"start": v(58.62, 109.34) * mm, "end": v(58.62, 112.51) * mm});
            skLineSegment(sketch, "E593.bottom", {"start": v(58.62, 112.51) * mm, "end": v(64.97, 112.51) * mm});
            skLineSegment(sketch, "E594.right", {"start": v(64.97, 109.34) * mm, "end": v(64.97, 112.51) * mm});
            skLineSegment(sketch, "E595.right", {"start": v(31.63, 109.34) * mm, "end": v(31.63, 112.51) * mm});
            skLineSegment(sketch, "E596.bottom", {"start": v(31.63, 112.51) * mm, "end": v(37.98, 112.51) * mm});
            skLineSegment(sketch, "E597.right", {"start": v(37.98, 109.34) * mm, "end": v(37.98, 112.51) * mm});
            skLineSegment(sketch, "E598.left", {"start": v(172.13, 109.34) * mm, "end": v(172.13, 112.51) * mm});
            skLineSegment(sketch, "E599.top", {"start": v(172.13, 112.51) * mm, "end": v(178.48, 112.51) * mm});
            skLineSegment(sketch, "E600.right", {"start": v(178.48, 109.34) * mm, "end": v(178.48, 112.51) * mm});
            skLineSegment(sketch, "E601.right", {"start": v(133.23, 109.34) * mm, "end": v(133.23, 112.51) * mm});
            skLineSegment(sketch, "E602.bottom", {"start": v(133.23, 112.51) * mm, "end": v(139.58, 112.51) * mm});
            skLineSegment(sketch, "E603.right", {"start": v(139.58, 109.34) * mm, "end": v(139.58, 112.51) * mm});
            skLineSegment(sketch, "E604.right", {"start": v(106.24, 109.34) * mm, "end": v(106.24, 112.51) * mm});
            skLineSegment(sketch, "E605.bottom", {"start": v(106.24, 112.51) * mm, "end": v(112.6, 112.51) * mm});
            skLineSegment(sketch, "E606.right", {"start": v(112.6, 109.34) * mm, "end": v(112.6, 112.51) * mm});
            skLineSegment(sketch, "E607", {"start": v(178.48, 109.34) * mm, "end": v(172.13, 109.34) * mm});
            skLineSegment(sketch, "E608", {"start": v(139.58, 109.34) * mm, "end": v(133.23, 109.34) * mm});
            skLineSegment(sketch, "E609", {"start": v(112.6, 109.34) * mm, "end": v(106.24, 109.34) * mm});
            skLineSegment(sketch, "E610", {"start": v(0.68, 109.34) * mm, "end": v(-5.67, 109.34) * mm});
            skLineSegment(sketch, "E611", {"start": v(-5.67, 112.51) * mm, "end": v(0.68, 112.51) * mm});
            skLineSegment(sketch, "E612", {"start": v(0.68, 112.51) * mm, "end": v(0.68, 109.34) * mm});
            skLineSegment(sketch, "E613", {"start": v(10.2, -208.16) * mm, "end": v(13.38, -208.16) * mm});
            skLineSegment(sketch, "E614", {"start": v(13.38, -208.16) * mm, "end": v(13.38, -201.81) * mm});
            skLineSegment(sketch, "E615", {"start": v(13.38, -201.81) * mm, "end": v(10.2, -201.81) * mm});
            skLineSegment(sketch, "E616", {"start": v(10.2, 122.04) * mm, "end": v(13.38, 122.04) * mm});
            skLineSegment(sketch, "E617", {"start": v(13.38, 122.04) * mm, "end": v(13.38, 128.39) * mm});
            skLineSegment(sketch, "E618", {"start": v(13.38, 128.39) * mm, "end": v(10.2, 128.39) * mm});
            skLineSegment(sketch, "E619", {"start": v(10.2, 93.46) * mm, "end": v(13.38, 93.46) * mm});
            skLineSegment(sketch, "E620", {"start": v(13.38, 93.46) * mm, "end": v(13.38, 99.81) * mm});
            skLineSegment(sketch, "E621", {"start": v(13.38, 99.81) * mm, "end": v(10.2, 99.81) * mm});
            skLineSegment(sketch, "E622", {"start": v(10.2, -88.57) * mm, "end": v(13.38, -88.57) * mm});
            skLineSegment(sketch, "E623", {"start": v(13.38, -88.57) * mm, "end": v(13.38, -82.22) * mm});
            skLineSegment(sketch, "E624", {"start": v(13.38, -82.22) * mm, "end": v(10.2, -82.22) * mm});
            skLineSegment(sketch, "E625", {"start": v(10.2, 2.44) * mm, "end": v(13.38, 2.44) * mm});
            skLineSegment(sketch, "E626", {"start": v(13.38, 2.44) * mm, "end": v(13.38, 8.8) * mm});
            skLineSegment(sketch, "E627", {"start": v(13.38, 8.8) * mm, "end": v(10.2, 8.8) * mm});
            skLineSegment(sketch, "E628", {"start": v(10.2, -43.06) * mm, "end": v(13.38, -43.06) * mm});
            skLineSegment(sketch, "E629", {"start": v(13.38, -43.06) * mm, "end": v(13.38, -36.71) * mm});
            skLineSegment(sketch, "E630", {"start": v(13.38, -36.71) * mm, "end": v(10.2, -36.71) * mm});
            skLineSegment(sketch, "E631", {"start": v(10.2, -179.59) * mm, "end": v(13.38, -179.59) * mm});
            skLineSegment(sketch, "E632", {"start": v(13.38, -179.59) * mm, "end": v(13.38, -173.24) * mm});
            skLineSegment(sketch, "E633", {"start": v(13.38, -173.24) * mm, "end": v(10.2, -173.24) * mm});
            skLineSegment(sketch, "E634", {"start": v(10.2, -134.08) * mm, "end": v(13.38, -134.08) * mm});
            skLineSegment(sketch, "E635", {"start": v(13.38, -134.08) * mm, "end": v(13.38, -127.73) * mm});
            skLineSegment(sketch, "E636", {"start": v(13.38, -127.73) * mm, "end": v(10.2, -127.73) * mm});
            skLineSegment(sketch, "E637", {"start": v(10.2, 47.95) * mm, "end": v(13.38, 47.95) * mm});
            skLineSegment(sketch, "E638", {"start": v(13.38, 47.95) * mm, "end": v(13.38, 54.3) * mm});
            skLineSegment(sketch, "E639", {"start": v(13.38, 54.3) * mm, "end": v(10.2, 54.3) * mm});
            skLineSegment(sketch, "E640", {"start": v(-18.37, -217.69) * mm, "end": v(-18.37, 137.91) * mm});
            skLineSegment(sketch, "E641", {"start": v(-18.37, -208.16) * mm, "end": v(-15.2, -208.16) * mm});
            skLineSegment(sketch, "E642", {"start": v(-15.2, -208.16) * mm, "end": v(-15.2, -201.81) * mm});
            skLineSegment(sketch, "E643", {"start": v(-15.2, -201.81) * mm, "end": v(-18.37, -201.81) * mm});
            skLineSegment(sketch, "E644", {"start": v(-18.37, -201.81) * mm, "end": v(-18.37, -192.29) * mm});
            skLineSegment(sketch, "E645", {"start": v(-18.37, 112.51) * mm, "end": v(-18.37, 122.04) * mm});
            skLineSegment(sketch, "E646", {"start": v(-18.37, 122.04) * mm, "end": v(-15.2, 122.04) * mm});
            skLineSegment(sketch, "E647", {"start": v(-15.2, 122.04) * mm, "end": v(-15.2, 128.39) * mm});
            skLineSegment(sketch, "E648", {"start": v(-15.2, 128.39) * mm, "end": v(-18.37, 128.39) * mm});
            skLineSegment(sketch, "E649", {"start": v(-18.37, 93.46) * mm, "end": v(-15.2, 93.46) * mm});
            skLineSegment(sketch, "E650", {"start": v(-15.2, 93.46) * mm, "end": v(-15.2, 99.81) * mm});
            skLineSegment(sketch, "E651", {"start": v(-15.2, 99.81) * mm, "end": v(-18.37, 99.81) * mm});
            skLineSegment(sketch, "E652", {"start": v(-18.37, -88.57) * mm, "end": v(-15.2, -88.57) * mm});
            skLineSegment(sketch, "E653", {"start": v(-15.2, -88.57) * mm, "end": v(-15.2, -82.22) * mm});
            skLineSegment(sketch, "E654", {"start": v(-15.2, -82.22) * mm, "end": v(-18.37, -82.22) * mm});
            skLineSegment(sketch, "E655", {"start": v(-18.37, 2.44) * mm, "end": v(-15.2, 2.44) * mm});
            skLineSegment(sketch, "E656", {"start": v(-15.2, 2.44) * mm, "end": v(-15.2, 8.8) * mm});
            skLineSegment(sketch, "E657", {"start": v(-15.2, 8.8) * mm, "end": v(-18.37, 8.8) * mm});
            skLineSegment(sketch, "E658", {"start": v(-18.37, -43.06) * mm, "end": v(-15.2, -43.06) * mm});
            skLineSegment(sketch, "E659", {"start": v(-15.2, -43.06) * mm, "end": v(-15.2, -36.71) * mm});
            skLineSegment(sketch, "E660", {"start": v(-15.2, -36.71) * mm, "end": v(-18.37, -36.71) * mm});
            skLineSegment(sketch, "E661", {"start": v(-18.37, -179.59) * mm, "end": v(-15.2, -179.59) * mm});
            skLineSegment(sketch, "E662", {"start": v(-15.2, -179.59) * mm, "end": v(-15.2, -173.24) * mm});
            skLineSegment(sketch, "E663", {"start": v(-15.2, -173.24) * mm, "end": v(-18.37, -173.24) * mm});
            skLineSegment(sketch, "E664", {"start": v(-18.37, -189.11) * mm, "end": v(-18.37, -179.59) * mm});
            skLineSegment(sketch, "E665", {"start": v(-18.37, -82.22) * mm, "end": v(-18.37, -43.06) * mm});
            skLineSegment(sketch, "E666", {"start": v(-18.37, -36.71) * mm, "end": v(-18.37, 2.44) * mm});
            skLineSegment(sketch, "E667", {"start": v(-18.37, 99.81) * mm, "end": v(-18.37, 109.34) * mm});
            skLineSegment(sketch, "E668", {"start": v(-18.37, -134.08) * mm, "end": v(-15.2, -134.08) * mm});
            skLineSegment(sketch, "E669", {"start": v(-15.2, -134.08) * mm, "end": v(-15.2, -127.73) * mm});
            skLineSegment(sketch, "E670", {"start": v(-15.2, -127.73) * mm, "end": v(-18.37, -127.73) * mm});
            skLineSegment(sketch, "E671", {"start": v(-18.37, 47.95) * mm, "end": v(-15.2, 47.95) * mm});
            skLineSegment(sketch, "E672", {"start": v(-15.2, 47.95) * mm, "end": v(-15.2, 54.3) * mm});
            skLineSegment(sketch, "E673", {"start": v(-15.2, 54.3) * mm, "end": v(-18.37, 54.3) * mm});
            skLineSegment(sketch, "E674", {"start": v(-18.37, 8.8) * mm, "end": v(-18.37, 47.95) * mm});
            skLineSegment(sketch, "E675", {"start": v(-18.37, 54.3) * mm, "end": v(-18.37, 93.46) * mm});
            skLineSegment(sketch, "E676", {"start": v(-18.37, -173.24) * mm, "end": v(-18.37, -134.08) * mm});
            skLineSegment(sketch, "E677", {"start": v(-18.37, -127.73) * mm, "end": v(-18.37, -88.57) * mm});
            skLineSegment(sketch, "E678", {"start": v(-18.37, 112.51) * mm, "end": v(-18.37, 109.34) * mm});
            skLineSegment(sketch, "E679", {"start": v(-18.37, -192.29) * mm, "end": v(-18.37, -189.11) * mm});
            skLineSegment(sketch, "E680", {"start": v(-18.37, 128.39) * mm, "end": v(-18.37, -208.16) * mm});
            skLineSegment(sketch, "E681", {"start": v(191.18, -217.69) * mm, "end": v(191.18, 137.91) * mm});
            skLineSegment(sketch, "E682", {"start": v(191.18, 128.39) * mm, "end": v(188, 128.39) * mm});
            skLineSegment(sketch, "E683", {"start": v(188, 128.39) * mm, "end": v(188, 122.04) * mm});
            skLineSegment(sketch, "E684", {"start": v(188, 122.04) * mm, "end": v(191.18, 122.04) * mm});
            skLineSegment(sketch, "E685", {"start": v(191.18, 122.04) * mm, "end": v(191.18, 112.51) * mm});
            skLineSegment(sketch, "E686", {"start": v(191.18, -192.29) * mm, "end": v(191.18, -201.81) * mm});
            skLineSegment(sketch, "E687", {"start": v(191.18, -201.81) * mm, "end": v(188, -201.81) * mm});
            skLineSegment(sketch, "E688", {"start": v(188, -201.81) * mm, "end": v(188, -208.16) * mm});
            skLineSegment(sketch, "E689", {"start": v(188, -208.16) * mm, "end": v(191.18, -208.16) * mm});
            skLineSegment(sketch, "E690", {"start": v(191.18, -173.24) * mm, "end": v(188, -173.24) * mm});
            skLineSegment(sketch, "E691", {"start": v(188, -173.24) * mm, "end": v(188, -179.59) * mm});
            skLineSegment(sketch, "E692", {"start": v(188, -179.59) * mm, "end": v(191.18, -179.59) * mm});
            skLineSegment(sketch, "E693", {"start": v(191.18, 8.8) * mm, "end": v(188, 8.8) * mm});
            skLineSegment(sketch, "E694", {"start": v(188, 8.8) * mm, "end": v(188, 2.44) * mm});
            skLineSegment(sketch, "E695", {"start": v(188, 2.44) * mm, "end": v(191.18, 2.44) * mm});
            skLineSegment(sketch, "E696", {"start": v(191.18, -82.22) * mm, "end": v(188, -82.22) * mm});
            skLineSegment(sketch, "E697", {"start": v(188, -82.22) * mm, "end": v(188, -88.57) * mm});
            skLineSegment(sketch, "E698", {"start": v(188, -88.57) * mm, "end": v(191.18, -88.57) * mm});
            skLineSegment(sketch, "E699", {"start": v(191.18, -36.71) * mm, "end": v(188, -36.71) * mm});
            skLineSegment(sketch, "E700", {"start": v(188, -36.71) * mm, "end": v(188, -43.06) * mm});
            skLineSegment(sketch, "E701", {"start": v(188, -43.06) * mm, "end": v(191.18, -43.06) * mm});
            skLineSegment(sketch, "E702", {"start": v(191.18, 99.81) * mm, "end": v(188, 99.81) * mm});
            skLineSegment(sketch, "E703", {"start": v(188, 99.81) * mm, "end": v(188, 93.46) * mm});
            skLineSegment(sketch, "E704", {"start": v(188, 93.46) * mm, "end": v(191.18, 93.46) * mm});
            skLineSegment(sketch, "E705", {"start": v(191.18, 109.34) * mm, "end": v(191.18, 99.81) * mm});
            skLineSegment(sketch, "E706", {"start": v(191.18, 2.44) * mm, "end": v(191.18, -36.71) * mm});
            skLineSegment(sketch, "E707", {"start": v(191.18, -43.06) * mm, "end": v(191.18, -82.22) * mm});
            skLineSegment(sketch, "E708", {"start": v(191.18, -179.59) * mm, "end": v(191.18, -189.11) * mm});
            skLineSegment(sketch, "E709", {"start": v(191.18, 54.3) * mm, "end": v(188, 54.3) * mm});
            skLineSegment(sketch, "E710", {"start": v(188, 54.3) * mm, "end": v(188, 47.95) * mm});
            skLineSegment(sketch, "E711", {"start": v(188, 47.95) * mm, "end": v(191.18, 47.95) * mm});
            skLineSegment(sketch, "E712", {"start": v(191.18, -127.73) * mm, "end": v(188, -127.73) * mm});
            skLineSegment(sketch, "E713", {"start": v(188, -127.73) * mm, "end": v(188, -134.08) * mm});
            skLineSegment(sketch, "E714", {"start": v(188, -134.08) * mm, "end": v(191.18, -134.08) * mm});
            skLineSegment(sketch, "E715", {"start": v(191.18, -88.57) * mm, "end": v(191.18, -127.73) * mm});
            skLineSegment(sketch, "E716", {"start": v(191.18, -134.08) * mm, "end": v(191.18, -173.24) * mm});
            skLineSegment(sketch, "E717", {"start": v(191.18, 93.46) * mm, "end": v(191.18, 54.3) * mm});
            skLineSegment(sketch, "E718", {"start": v(191.18, 47.95) * mm, "end": v(191.18, 8.8) * mm});
            skLineSegment(sketch, "E719", {"start": v(191.18, -192.29) * mm, "end": v(191.18, -189.11) * mm});
            skLineSegment(sketch, "E720", {"start": v(191.18, 112.51) * mm, "end": v(191.18, 109.34) * mm});
            skLineSegment(sketch, "E721", {"start": v(191.18, -208.16) * mm, "end": v(191.18, 128.39) * mm});
            skLineSegment(sketch, "E722", {"start": v(159.43, -208.16) * mm, "end": v(162.6, -208.16) * mm});
            skLineSegment(sketch, "E723", {"start": v(162.6, -208.16) * mm, "end": v(162.6, -201.81) * mm});
            skLineSegment(sketch, "E724", {"start": v(162.6, -201.81) * mm, "end": v(159.43, -201.81) * mm});
            skLineSegment(sketch, "E725", {"start": v(159.43, 122.04) * mm, "end": v(162.6, 122.04) * mm});
            skLineSegment(sketch, "E726", {"start": v(162.6, 122.04) * mm, "end": v(162.6, 128.39) * mm});
            skLineSegment(sketch, "E727", {"start": v(162.6, 128.39) * mm, "end": v(159.43, 128.39) * mm});
            skLineSegment(sketch, "E728", {"start": v(159.39, 93.45) * mm, "end": v(162.56, 93.45) * mm});
            skLineSegment(sketch, "E729", {"start": v(162.56, 93.45) * mm, "end": v(162.56, 99.8) * mm});
            skLineSegment(sketch, "E730", {"start": v(162.56, 99.8) * mm, "end": v(159.39, 99.8) * mm});
            skLineSegment(sketch, "E731", {"start": v(159.39, -88.58) * mm, "end": v(162.56, -88.58) * mm});
            skLineSegment(sketch, "E732", {"start": v(162.56, -88.58) * mm, "end": v(162.56, -82.23) * mm});
            skLineSegment(sketch, "E733", {"start": v(162.56, -82.23) * mm, "end": v(159.39, -82.23) * mm});
            skLineSegment(sketch, "E734", {"start": v(159.39, 2.43) * mm, "end": v(162.56, 2.43) * mm});
            skLineSegment(sketch, "E735", {"start": v(162.56, 2.43) * mm, "end": v(162.56, 8.78) * mm});
            skLineSegment(sketch, "E736", {"start": v(162.56, 8.78) * mm, "end": v(159.39, 8.78) * mm});
            skLineSegment(sketch, "E737", {"start": v(159.39, -43.07) * mm, "end": v(162.56, -43.07) * mm});
            skLineSegment(sketch, "E738", {"start": v(162.56, -43.07) * mm, "end": v(162.56, -36.72) * mm});
            skLineSegment(sketch, "E739", {"start": v(162.56, -36.72) * mm, "end": v(159.39, -36.72) * mm});
            skLineSegment(sketch, "E740", {"start": v(159.39, -179.6) * mm, "end": v(162.56, -179.6) * mm});
            skLineSegment(sketch, "E741", {"start": v(162.56, -179.6) * mm, "end": v(162.56, -173.25) * mm});
            skLineSegment(sketch, "E742", {"start": v(162.56, -173.25) * mm, "end": v(159.39, -173.25) * mm});
            skLineSegment(sketch, "E743", {"start": v(159.39, -134.1) * mm, "end": v(162.56, -134.1) * mm});
            skLineSegment(sketch, "E744", {"start": v(162.56, -134.1) * mm, "end": v(162.56, -127.74) * mm});
            skLineSegment(sketch, "E745", {"start": v(162.56, -127.74) * mm, "end": v(159.39, -127.74) * mm});
            skLineSegment(sketch, "E746", {"start": v(159.39, 47.94) * mm, "end": v(162.56, 47.94) * mm});
            skLineSegment(sketch, "E747", {"start": v(162.56, 47.94) * mm, "end": v(162.56, 54.3) * mm});
            skLineSegment(sketch, "E748", {"start": v(162.56, 54.3) * mm, "end": v(159.39, 54.3) * mm});
            skLineSegment(sketch, "E749", {"start": v(84.82, -208.16) * mm, "end": v(88, -208.16) * mm});
            skLineSegment(sketch, "E750", {"start": v(88, -208.16) * mm, "end": v(88, -201.81) * mm});
            skLineSegment(sketch, "E751", {"start": v(88, -201.81) * mm, "end": v(84.82, -201.81) * mm});
            skLineSegment(sketch, "E752", {"start": v(84.82, 122.04) * mm, "end": v(88, 122.04) * mm});
            skLineSegment(sketch, "E753", {"start": v(88, 122.04) * mm, "end": v(88, 128.39) * mm});
            skLineSegment(sketch, "E754", {"start": v(88, 128.39) * mm, "end": v(84.82, 128.39) * mm});
            skLineSegment(sketch, "E755", {"start": v(84.8, 93.45) * mm, "end": v(87.97, 93.45) * mm});
            skLineSegment(sketch, "E756", {"start": v(87.97, 93.45) * mm, "end": v(87.97, 99.8) * mm});
            skLineSegment(sketch, "E757", {"start": v(87.97, 99.8) * mm, "end": v(84.8, 99.8) * mm});
            skLineSegment(sketch, "E758", {"start": v(84.8, -88.58) * mm, "end": v(87.97, -88.58) * mm});
            skLineSegment(sketch, "E759", {"start": v(87.97, -88.58) * mm, "end": v(87.97, -82.23) * mm});
            skLineSegment(sketch, "E760", {"start": v(87.97, -82.23) * mm, "end": v(84.8, -82.23) * mm});
            skLineSegment(sketch, "E761", {"start": v(84.8, 2.43) * mm, "end": v(87.97, 2.43) * mm});
            skLineSegment(sketch, "E762", {"start": v(87.97, 2.43) * mm, "end": v(87.97, 8.78) * mm});
            skLineSegment(sketch, "E763", {"start": v(87.97, 8.78) * mm, "end": v(84.8, 8.78) * mm});
            skLineSegment(sketch, "E764", {"start": v(84.8, -43.07) * mm, "end": v(87.97, -43.07) * mm});
            skLineSegment(sketch, "E765", {"start": v(87.97, -43.07) * mm, "end": v(87.97, -36.72) * mm});
            skLineSegment(sketch, "E766", {"start": v(87.97, -36.72) * mm, "end": v(84.8, -36.72) * mm});
            skLineSegment(sketch, "E767", {"start": v(84.8, -179.6) * mm, "end": v(87.97, -179.6) * mm});
            skLineSegment(sketch, "E768", {"start": v(87.97, -179.6) * mm, "end": v(87.97, -173.25) * mm});
            skLineSegment(sketch, "E769", {"start": v(87.97, -173.25) * mm, "end": v(84.8, -173.25) * mm});
            skLineSegment(sketch, "E770", {"start": v(84.8, -134.1) * mm, "end": v(87.97, -134.1) * mm});
            skLineSegment(sketch, "E771", {"start": v(87.97, -134.1) * mm, "end": v(87.97, -127.74) * mm});
            skLineSegment(sketch, "E772", {"start": v(87.97, -127.74) * mm, "end": v(84.8, -127.74) * mm});
            skLineSegment(sketch, "E773", {"start": v(84.8, 47.94) * mm, "end": v(87.97, 47.94) * mm});
            skLineSegment(sketch, "E774", {"start": v(87.97, 47.94) * mm, "end": v(87.97, 54.3) * mm});
            skLineSegment(sketch, "E775", {"start": v(87.97, 54.3) * mm, "end": v(84.8, 54.3) * mm});
            skLineSegment(sketch, "E776.bottom", {"start": v(19.73, 109.34) * mm, "end": v(84.8, 109.34) * mm});
            skLineSegment(sketch, "E776.top", {"start": v(19.73, -189.11) * mm, "end": v(84.8, -189.11) * mm});
            skLineSegment(sketch, "E776.left", {"start": v(19.73, 109.34) * mm, "end": v(19.73, -189.11) * mm});
            skLineSegment(sketch, "E776.right", {"start": v(84.8, 109.34) * mm, "end": v(84.8, -189.11) * mm});
            skLineSegment(sketch, "E777.left", {"start": v(94.32, 102.98) * mm, "end": v(94.32, -189.11) * mm});
            skLineSegment(sketch, "E777.right", {"start": v(159.39, 102.98) * mm, "end": v(159.39, -182.77) * mm});
            skLineSegment(sketch, "E778.top", {"start": v(94.32, -189.12) * mm, "end": v(159.39, -189.12) * mm});
            skLineSegment(sketch, "E779", {"start": v(94.32, -189.11) * mm, "end": v(94.32, -189.12) * mm});
            skLineSegment(sketch, "E780", {"start": v(159.39, -182.77) * mm, "end": v(159.39, -189.12) * mm});
            skLineSegment(sketch, "E781.bottom", {"start": v(94.32, 109.33) * mm, "end": v(159.39, 109.33) * mm});
            skLineSegment(sketch, "E782", {"start": v(94.32, 102.98) * mm, "end": v(94.32, 109.33) * mm});
            skLineSegment(sketch, "E783", {"start": v(159.39, 109.33) * mm, "end": v(159.39, 102.98) * mm});
            skLineSegment(sketch, "E784", {"start": v(159.43, 128.39) * mm, "end": v(159.43, 122.04) * mm});
            skLineSegment(sketch, "E785", {"start": v(159.43, -201.81) * mm, "end": v(159.43, -208.16) * mm});
            skLineSegment(sketch, "E786", {"start": v(84.82, -201.81) * mm, "end": v(84.82, -208.16) * mm});
            skLineSegment(sketch, "E787", {"start": v(84.82, 128.39) * mm, "end": v(84.82, 122.04) * mm});
            skLineSegment(sketch, "E788", {"start": v(10.2, -173.24) * mm, "end": v(10.2, -179.59) * mm});
            skLineSegment(sketch, "E789", {"start": v(10.2, -201.81) * mm, "end": v(10.2, -208.16) * mm});
            skLineSegment(sketch, "E790", {"start": v(10.2, -127.73) * mm, "end": v(10.2, -134.08) * mm});
            skLineSegment(sketch, "E791", {"start": v(10.2, -82.22) * mm, "end": v(10.2, -88.57) * mm});
            skLineSegment(sketch, "E792", {"start": v(10.2, -36.71) * mm, "end": v(10.2, -43.06) * mm});
            skLineSegment(sketch, "E793", {"start": v(10.2, 8.8) * mm, "end": v(10.2, 2.44) * mm});
            skLineSegment(sketch, "E794", {"start": v(10.2, 54.3) * mm, "end": v(10.2, 47.95) * mm});
            skLineSegment(sketch, "E795", {"start": v(10.2, 99.81) * mm, "end": v(10.2, 93.46) * mm});
            skLineSegment(sketch, "E796", {"start": v(10.2, 128.39) * mm, "end": v(10.2, 122.04) * mm});
            skSolve(sketch);
        }
        {
            var Q0;
            {var subQ35=sQuery(id+"F10.wireOp",EDGE,"E570.bottom");Q0=makeQuery(id+"F10.imprint","IMPRINT",FACE,{"disambiguationData":[TD([[makeQuery(id+"F10.imprint","IMPRINT",EDGE,{"derivedFrom":subQ35}),1.0]])]});}
            extrude(context, id + "F11", {"entities" : qUnion([Q0]), "depth" : 3.17 * mm, "offsetDistance" : 25.4 * mm});
        }
        {
            var Q0;
            Q0=makeQuery(id+"F9.opExtrude","CAP_FACE",FACE,{"disambiguationData":[OSD([sQuery(id+"F8.wireOp",EDGE,"E328.bottom"),sQuery(id+"F8.wireOp",EDGE,"E328.top"),sQuery(id+"F8.wireOp",EDGE,"E329.left"),sQuery(id+"F8.wireOp",EDGE,"E330.right"),sQuery(id+"F8.wireOp",EDGE,"E331.bottom"),sQuery(id+"F8.wireOp",EDGE,"E332.right"),sQuery(id+"F8.wireOp",EDGE,"E333.right"),sQuery(id+"F8.wireOp",EDGE,"E334.bottom"),sQuery(id+"F8.wireOp",EDGE,"E335.right"),sQuery(id+"F8.wireOp",EDGE,"E336.left"),sQuery(id+"F8.wireOp",EDGE,"E337.top"),sQuery(id+"F8.wireOp",EDGE,"E338.right"),sQuery(id+"F8.wireOp",EDGE,"E339.right"),sQuery(id+"F8.wireOp",EDGE,"E340.bottom"),sQuery(id+"F8.wireOp",EDGE,"E341.right"),sQuery(id+"F8.wireOp",EDGE,"E342.right"),sQuery(id+"F8.wireOp",EDGE,"E343.bottom"),sQuery(id+"F8.wireOp",EDGE,"E344.right"),sQuery(id+"F8.wireOp",EDGE,"E345"),sQuery(id+"F8.wireOp",EDGE,"E346"),sQuery(id+"F8.wireOp",EDGE,"E347"),sQuery(id+"F8.wireOp",EDGE,"E348"),sQuery(id+"F8.wireOp",EDGE,"E349"),sQuery(id+"F8.wireOp",EDGE,"E350"),sQuery(id+"F8.wireOp",EDGE,"E351"),sQuery(id+"F8.wireOp",EDGE,"E352"),sQuery(id+"F8.wireOp",EDGE,"E353.left"),sQuery(id+"F8.wireOp",EDGE,"E354.right"),sQuery(id+"F8.wireOp",EDGE,"E355.bottom"),sQuery(id+"F8.wireOp",EDGE,"E356.right"),sQuery(id+"F8.wireOp",EDGE,"E357.right"),sQuery(id+"F8.wireOp",EDGE,"E358.bottom"),sQuery(id+"F8.wireOp",EDGE,"E359.right"),sQuery(id+"F8.wireOp",EDGE,"E360.left"),sQuery(id+"F8.wireOp",EDGE,"E361.top"),sQuery(id+"F8.wireOp",EDGE,"E362.right"),sQuery(id+"F8.wireOp",EDGE,"E363.right"),sQuery(id+"F8.wireOp",EDGE,"E364.bottom"),sQuery(id+"F8.wireOp",EDGE,"E365.right"),sQuery(id+"F8.wireOp",EDGE,"E366.right"),sQuery(id+"F8.wireOp",EDGE,"E367.bottom"),sQuery(id+"F8.wireOp",EDGE,"E368.right"),sQuery(id+"F8.wireOp",EDGE,"E369"),sQuery(id+"F8.wireOp",EDGE,"E370"),sQuery(id+"F8.wireOp",EDGE,"E371"),sQuery(id+"F8.wireOp",EDGE,"E372"),sQuery(id+"F8.wireOp",EDGE,"E373"),sQuery(id+"F8.wireOp",EDGE,"E374"),sQuery(id+"F8.wireOp",EDGE,"E375"),sQuery(id+"F8.wireOp",EDGE,"E376"),sQuery(id+"F8.wireOp",EDGE,"E378"),sQuery(id+"F8.wireOp",EDGE,"E379"),sQuery(id+"F8.wireOp",EDGE,"E380"),sQuery(id+"F8.wireOp",EDGE,"E381"),sQuery(id+"F8.wireOp",EDGE,"E382"),sQuery(id+"F8.wireOp",EDGE,"E383"),sQuery(id+"F8.wireOp",EDGE,"E384"),sQuery(id+"F8.wireOp",EDGE,"E385"),sQuery(id+"F8.wireOp",EDGE,"E386"),sQuery(id+"F8.wireOp",EDGE,"E387"),sQuery(id+"F8.wireOp",EDGE,"E388"),sQuery(id+"F8.wireOp",EDGE,"E389"),sQuery(id+"F8.wireOp",EDGE,"E390"),sQuery(id+"F8.wireOp",EDGE,"E391"),sQuery(id+"F8.wireOp",EDGE,"E392"),sQuery(id+"F8.wireOp",EDGE,"E393"),sQuery(id+"F8.wireOp",EDGE,"E394"),sQuery(id+"F8.wireOp",EDGE,"E395"),sQuery(id+"F8.wireOp",EDGE,"E396"),sQuery(id+"F8.wireOp",EDGE,"E397"),sQuery(id+"F8.wireOp",EDGE,"E398"),sQuery(id+"F8.wireOp",EDGE,"E399"),sQuery(id+"F8.wireOp",EDGE,"E400"),sQuery(id+"F8.wireOp",EDGE,"E401"),sQuery(id+"F8.wireOp",EDGE,"E402"),sQuery(id+"F8.wireOp",EDGE,"E403"),sQuery(id+"F8.wireOp",EDGE,"E404"),sQuery(id+"F8.wireOp",EDGE,"E406"),sQuery(id+"F8.wireOp",EDGE,"E407"),sQuery(id+"F8.wireOp",EDGE,"E408"),sQuery(id+"F8.wireOp",EDGE,"E409"),sQuery(id+"F8.wireOp",EDGE,"E410"),sQuery(id+"F8.wireOp",EDGE,"E411"),sQuery(id+"F8.wireOp",EDGE,"E412"),sQuery(id+"F8.wireOp",EDGE,"E413"),sQuery(id+"F8.wireOp",EDGE,"E414"),sQuery(id+"F8.wireOp",EDGE,"E415"),sQuery(id+"F8.wireOp",EDGE,"E416"),sQuery(id+"F8.wireOp",EDGE,"E417"),sQuery(id+"F8.wireOp",EDGE,"E418"),sQuery(id+"F8.wireOp",EDGE,"E419"),sQuery(id+"F8.wireOp",EDGE,"E420"),sQuery(id+"F8.wireOp",EDGE,"E421"),sQuery(id+"F8.wireOp",EDGE,"E422"),sQuery(id+"F8.wireOp",EDGE,"E423"),sQuery(id+"F8.wireOp",EDGE,"E424"),sQuery(id+"F8.wireOp",EDGE,"E425"),sQuery(id+"F8.wireOp",EDGE,"E426"),sQuery(id+"F8.wireOp",EDGE,"E427"),sQuery(id+"F8.wireOp",EDGE,"E428"),sQuery(id+"F8.wireOp",EDGE,"E429"),sQuery(id+"F8.wireOp",EDGE,"E430"),sQuery(id+"F8.wireOp",EDGE,"E431"),sQuery(id+"F8.wireOp",EDGE,"E432"),sQuery(id+"F8.wireOp",EDGE,"E433"),sQuery(id+"F8.wireOp",EDGE,"E434"),sQuery(id+"F8.wireOp",EDGE,"E435"),sQuery(id+"F8.wireOp",EDGE,"E436"),sQuery(id+"F8.wireOp",EDGE,"E437"),sQuery(id+"F8.wireOp",EDGE,"E438"),sQuery(id+"F8.wireOp",EDGE,"E439"),sQuery(id+"F8.wireOp",EDGE,"E440"),sQuery(id+"F8.wireOp",EDGE,"E441"),sQuery(id+"F8.wireOp",EDGE,"E442"),sQuery(id+"F8.wireOp",EDGE,"E443"),sQuery(id+"F8.wireOp",EDGE,"E444"),sQuery(id+"F8.wireOp",EDGE,"E445"),sQuery(id+"F8.wireOp",EDGE,"E446"),sQuery(id+"F8.wireOp",EDGE,"E447"),sQuery(id+"F8.wireOp",EDGE,"E448"),sQuery(id+"F8.wireOp",EDGE,"E449"),sQuery(id+"F8.wireOp",EDGE,"E450"),sQuery(id+"F8.wireOp",EDGE,"E451"),sQuery(id+"F8.wireOp",EDGE,"E452"),sQuery(id+"F8.wireOp",EDGE,"E453"),sQuery(id+"F8.wireOp",EDGE,"E454"),sQuery(id+"F8.wireOp",EDGE,"E455"),sQuery(id+"F8.wireOp",EDGE,"E456"),sQuery(id+"F8.wireOp",EDGE,"E457"),sQuery(id+"F8.wireOp",EDGE,"E458"),sQuery(id+"F8.wireOp",EDGE,"E459"),sQuery(id+"F8.wireOp",EDGE,"E460"),sQuery(id+"F8.wireOp",EDGE,"E461"),sQuery(id+"F8.wireOp",EDGE,"E462"),sQuery(id+"F8.wireOp",EDGE,"E463"),sQuery(id+"F8.wireOp",EDGE,"E464"),sQuery(id+"F8.wireOp",EDGE,"E465"),sQuery(id+"F8.wireOp",EDGE,"E466"),sQuery(id+"F8.wireOp",EDGE,"E467"),sQuery(id+"F8.wireOp",EDGE,"E468"),sQuery(id+"F8.wireOp",EDGE,"E469"),sQuery(id+"F8.wireOp",EDGE,"E470"),sQuery(id+"F8.wireOp",EDGE,"E471"),sQuery(id+"F8.wireOp",EDGE,"E472"),sQuery(id+"F8.wireOp",EDGE,"E473"),sQuery(id+"F8.wireOp",EDGE,"E474"),sQuery(id+"F8.wireOp",EDGE,"E475"),sQuery(id+"F8.wireOp",EDGE,"E476"),sQuery(id+"F8.wireOp",EDGE,"E477"),sQuery(id+"F8.wireOp",EDGE,"E478"),sQuery(id+"F8.wireOp",EDGE,"E479"),sQuery(id+"F8.wireOp",EDGE,"E480"),sQuery(id+"F8.wireOp",EDGE,"E481"),sQuery(id+"F8.wireOp",EDGE,"E482"),sQuery(id+"F8.wireOp",EDGE,"E483"),sQuery(id+"F8.wireOp",EDGE,"E484"),sQuery(id+"F8.wireOp",EDGE,"E485"),sQuery(id+"F8.wireOp",EDGE,"E486"),sQuery(id+"F8.wireOp",EDGE,"E487"),sQuery(id+"F8.wireOp",EDGE,"E488"),sQuery(id+"F8.wireOp",EDGE,"E489"),sQuery(id+"F8.wireOp",EDGE,"E490"),sQuery(id+"F8.wireOp",EDGE,"E491"),sQuery(id+"F8.wireOp",EDGE,"E492"),sQuery(id+"F8.wireOp",EDGE,"E493"),sQuery(id+"F8.wireOp",EDGE,"E494"),sQuery(id+"F8.wireOp",EDGE,"E495"),sQuery(id+"F8.wireOp",EDGE,"E496"),sQuery(id+"F8.wireOp",EDGE,"E497"),sQuery(id+"F8.wireOp",EDGE,"E498"),sQuery(id+"F8.wireOp",EDGE,"E499"),sQuery(id+"F8.wireOp",EDGE,"E500"),sQuery(id+"F8.wireOp",EDGE,"E501"),sQuery(id+"F8.wireOp",EDGE,"E502"),sQuery(id+"F8.wireOp",EDGE,"E503"),sQuery(id+"F8.wireOp",EDGE,"E504"),sQuery(id+"F8.wireOp",EDGE,"E505"),sQuery(id+"F8.wireOp",EDGE,"E506"),sQuery(id+"F8.wireOp",EDGE,"E507"),sQuery(id+"F8.wireOp",EDGE,"E508"),sQuery(id+"F8.wireOp",EDGE,"E510"),sQuery(id+"F8.wireOp",EDGE,"E511"),sQuery(id+"F8.wireOp",EDGE,"E512"),sQuery(id+"F8.wireOp",EDGE,"E513"),sQuery(id+"F8.wireOp",EDGE,"E514"),sQuery(id+"F8.wireOp",EDGE,"E515"),sQuery(id+"F8.wireOp",EDGE,"E516"),sQuery(id+"F8.wireOp",EDGE,"E517"),sQuery(id+"F8.wireOp",EDGE,"E518"),sQuery(id+"F8.wireOp",EDGE,"E519"),sQuery(id+"F8.wireOp",EDGE,"E520"),sQuery(id+"F8.wireOp",EDGE,"E521"),sQuery(id+"F8.wireOp",EDGE,"E522"),sQuery(id+"F8.wireOp",EDGE,"E523"),sQuery(id+"F8.wireOp",EDGE,"E524"),sQuery(id+"F8.wireOp",EDGE,"E525"),sQuery(id+"F8.wireOp",EDGE,"E526"),sQuery(id+"F8.wireOp",EDGE,"E527"),sQuery(id+"F8.wireOp",EDGE,"E528"),sQuery(id+"F8.wireOp",EDGE,"E529"),sQuery(id+"F8.wireOp",EDGE,"E530"),sQuery(id+"F8.wireOp",EDGE,"E531"),sQuery(id+"F8.wireOp",EDGE,"E532"),sQuery(id+"F8.wireOp",EDGE,"E533"),sQuery(id+"F8.wireOp",EDGE,"E534"),sQuery(id+"F8.wireOp",EDGE,"E535"),sQuery(id+"F8.wireOp",EDGE,"E536"),sQuery(id+"F8.wireOp",EDGE,"E537"),sQuery(id+"F8.wireOp",EDGE,"E538"),sQuery(id+"F8.wireOp",EDGE,"E539"),sQuery(id+"F8.wireOp",EDGE,"E540"),sQuery(id+"F8.wireOp",EDGE,"E541"),sQuery(id+"F8.wireOp",EDGE,"E542"),sQuery(id+"F8.wireOp",EDGE,"E543"),sQuery(id+"F8.wireOp",EDGE,"E544"),sQuery(id+"F8.wireOp",EDGE,"E545"),sQuery(id+"F8.wireOp",EDGE,"E546"),sQuery(id+"F8.wireOp",EDGE,"E547"),sQuery(id+"F8.wireOp",EDGE,"E548"),sQuery(id+"F8.wireOp",EDGE,"E549"),sQuery(id+"F8.wireOp",EDGE,"E550"),sQuery(id+"F8.wireOp",EDGE,"E551"),sQuery(id+"F8.wireOp",EDGE,"E552"),sQuery(id+"F8.wireOp",EDGE,"E553"),sQuery(id+"F8.wireOp",EDGE,"E554"),sQuery(id+"F8.wireOp",EDGE,"E555"),sQuery(id+"F8.wireOp",EDGE,"E556"),sQuery(id+"F8.wireOp",EDGE,"E557"),sQuery(id+"F8.wireOp",EDGE,"E558"),sQuery(id+"F8.wireOp",EDGE,"E559"),sQuery(id+"F8.wireOp",EDGE,"E560"),sQuery(id+"F8.wireOp",EDGE,"E561"),sQuery(id+"F8.wireOp",EDGE,"E562"),sQuery(id+"F8.wireOp",EDGE,"E563"),sQuery(id+"F8.wireOp",EDGE,"E564"),sQuery(id+"F8.wireOp",EDGE,"E565"),sQuery(id+"F8.wireOp",EDGE,"E566"),sQuery(id+"F8.wireOp",EDGE,"E567"),sQuery(id+"F8.wireOp",EDGE,"E568"),sQuery(id+"F8.wireOp",EDGE,"E569")])],"isStart":false});
            var sketch = newSketch(context, id + "F12", { "sketchPlane" : qUnion([Q0])});
            skLineSegment(sketch, "E797.bottom", {"start": v(191.83, 439.59) * mm, "end": v(-17.72, 439.59) * mm});
            skLineSegment(sketch, "E797.top", {"start": v(191.83, 395.14) * mm, "end": v(-17.72, 395.14) * mm});
            skLineSegment(sketch, "E798", {"start": v(10.85, 401.49) * mm, "end": v(14.03, 401.49) * mm});
            skLineSegment(sketch, "E799", {"start": v(14.03, 401.49) * mm, "end": v(14.03, 407.84) * mm});
            skLineSegment(sketch, "E800", {"start": v(14.03, 407.84) * mm, "end": v(10.85, 407.84) * mm});
            skLineSegment(sketch, "E801", {"start": v(-17.72, 401.49) * mm, "end": v(-14.55, 401.49) * mm});
            skLineSegment(sketch, "E802", {"start": v(-14.55, 401.49) * mm, "end": v(-14.55, 407.84) * mm});
            skLineSegment(sketch, "E803", {"start": v(-14.55, 407.84) * mm, "end": v(-17.72, 407.84) * mm});
            skLineSegment(sketch, "E804", {"start": v(191.83, 407.84) * mm, "end": v(188.65, 407.84) * mm});
            skLineSegment(sketch, "E805", {"start": v(188.65, 407.84) * mm, "end": v(188.65, 401.49) * mm});
            skLineSegment(sketch, "E806", {"start": v(188.65, 401.49) * mm, "end": v(191.83, 401.49) * mm});
            skLineSegment(sketch, "E807", {"start": v(160.08, 401.49) * mm, "end": v(163.25, 401.49) * mm});
            skLineSegment(sketch, "E808", {"start": v(163.25, 401.49) * mm, "end": v(163.25, 407.84) * mm});
            skLineSegment(sketch, "E809", {"start": v(163.25, 407.84) * mm, "end": v(160.08, 407.84) * mm});
            skLineSegment(sketch, "E810", {"start": v(85.46, 401.49) * mm, "end": v(88.64, 401.49) * mm});
            skLineSegment(sketch, "E811", {"start": v(88.64, 401.49) * mm, "end": v(88.64, 407.84) * mm});
            skLineSegment(sketch, "E812", {"start": v(88.64, 407.84) * mm, "end": v(85.46, 407.84) * mm});
            skLineSegment(sketch, "E813", {"start": v(10.85, 407.84) * mm, "end": v(10.85, 401.49) * mm});
            skLineSegment(sketch, "E814", {"start": v(85.46, 407.84) * mm, "end": v(85.46, 401.49) * mm});
            skLineSegment(sketch, "E815", {"start": v(160.08, 401.49) * mm, "end": v(160.08, 407.84) * mm});
            skLineSegment(sketch, "E816", {"start": v(10.85, 426.89) * mm, "end": v(14.03, 426.89) * mm});
            skLineSegment(sketch, "E817", {"start": v(14.03, 426.89) * mm, "end": v(14.03, 433.24) * mm});
            skLineSegment(sketch, "E818", {"start": v(14.03, 433.24) * mm, "end": v(10.85, 433.24) * mm});
            skLineSegment(sketch, "E819", {"start": v(-17.72, 426.89) * mm, "end": v(-14.55, 426.89) * mm});
            skLineSegment(sketch, "E820", {"start": v(-14.55, 426.89) * mm, "end": v(-14.55, 433.24) * mm});
            skLineSegment(sketch, "E821", {"start": v(-14.55, 433.24) * mm, "end": v(-17.72, 433.24) * mm});
            skLineSegment(sketch, "E822", {"start": v(191.83, 433.24) * mm, "end": v(188.65, 433.24) * mm});
            skLineSegment(sketch, "E823", {"start": v(188.65, 433.24) * mm, "end": v(188.65, 426.89) * mm});
            skLineSegment(sketch, "E824", {"start": v(188.65, 426.89) * mm, "end": v(191.83, 426.89) * mm});
            skLineSegment(sketch, "E825", {"start": v(160.08, 426.89) * mm, "end": v(163.25, 426.89) * mm});
            skLineSegment(sketch, "E826", {"start": v(163.25, 426.89) * mm, "end": v(163.25, 433.24) * mm});
            skLineSegment(sketch, "E827", {"start": v(163.25, 433.24) * mm, "end": v(160.08, 433.24) * mm});
            skLineSegment(sketch, "E828", {"start": v(85.46, 426.89) * mm, "end": v(88.64, 426.89) * mm});
            skLineSegment(sketch, "E829", {"start": v(88.64, 426.89) * mm, "end": v(88.64, 433.24) * mm});
            skLineSegment(sketch, "E830", {"start": v(88.64, 433.24) * mm, "end": v(85.46, 433.24) * mm});
            skLineSegment(sketch, "E831", {"start": v(10.85, 433.24) * mm, "end": v(10.85, 426.89) * mm});
            skLineSegment(sketch, "E832", {"start": v(85.46, 433.24) * mm, "end": v(85.46, 426.89) * mm});
            skLineSegment(sketch, "E833", {"start": v(160.08, 426.89) * mm, "end": v(160.08, 433.24) * mm});
            skLineSegment(sketch, "E834", {"start": v(191.83, 395.14) * mm, "end": v(191.83, 401.49) * mm});
            skLineSegment(sketch, "E835", {"start": v(191.83, 407.84) * mm, "end": v(191.83, 426.89) * mm});
            skLineSegment(sketch, "E836", {"start": v(191.83, 433.24) * mm, "end": v(191.83, 439.59) * mm});
            skLineSegment(sketch, "E837", {"start": v(-17.72, 439.59) * mm, "end": v(-17.72, 433.24) * mm});
            skLineSegment(sketch, "E838", {"start": v(-17.72, 426.89) * mm, "end": v(-17.72, 407.84) * mm});
            skLineSegment(sketch, "E839", {"start": v(-17.72, 401.49) * mm, "end": v(-17.72, 395.14) * mm});
            skSolve(sketch);
        }
        {
            var Q0;
            Q0 = qSketchRegion(id + "F12", true);
            extrude(context, id + "F13", {"entities" : qUnion([Q0]), "depth" : 3.17 * mm, "offsetDistance" : 25.4 * mm});
        }
        {
            var Q0;
            Q0=makeQuery(id+"F9.opExtrude","CAP_FACE",FACE,{"disambiguationData":[OSD([sQuery(id+"F8.wireOp",EDGE,"E328.bottom"),sQuery(id+"F8.wireOp",EDGE,"E328.top"),sQuery(id+"F8.wireOp",EDGE,"E329.left"),sQuery(id+"F8.wireOp",EDGE,"E330.right"),sQuery(id+"F8.wireOp",EDGE,"E331.bottom"),sQuery(id+"F8.wireOp",EDGE,"E332.right"),sQuery(id+"F8.wireOp",EDGE,"E333.right"),sQuery(id+"F8.wireOp",EDGE,"E334.bottom"),sQuery(id+"F8.wireOp",EDGE,"E335.right"),sQuery(id+"F8.wireOp",EDGE,"E336.left"),sQuery(id+"F8.wireOp",EDGE,"E337.top"),sQuery(id+"F8.wireOp",EDGE,"E338.right"),sQuery(id+"F8.wireOp",EDGE,"E339.right"),sQuery(id+"F8.wireOp",EDGE,"E340.bottom"),sQuery(id+"F8.wireOp",EDGE,"E341.right"),sQuery(id+"F8.wireOp",EDGE,"E342.right"),sQuery(id+"F8.wireOp",EDGE,"E343.bottom"),sQuery(id+"F8.wireOp",EDGE,"E344.right"),sQuery(id+"F8.wireOp",EDGE,"E345"),sQuery(id+"F8.wireOp",EDGE,"E346"),sQuery(id+"F8.wireOp",EDGE,"E347"),sQuery(id+"F8.wireOp",EDGE,"E348"),sQuery(id+"F8.wireOp",EDGE,"E349"),sQuery(id+"F8.wireOp",EDGE,"E350"),sQuery(id+"F8.wireOp",EDGE,"E351"),sQuery(id+"F8.wireOp",EDGE,"E352"),sQuery(id+"F8.wireOp",EDGE,"E353.left"),sQuery(id+"F8.wireOp",EDGE,"E354.right"),sQuery(id+"F8.wireOp",EDGE,"E355.bottom"),sQuery(id+"F8.wireOp",EDGE,"E356.right"),sQuery(id+"F8.wireOp",EDGE,"E357.right"),sQuery(id+"F8.wireOp",EDGE,"E358.bottom"),sQuery(id+"F8.wireOp",EDGE,"E359.right"),sQuery(id+"F8.wireOp",EDGE,"E360.left"),sQuery(id+"F8.wireOp",EDGE,"E361.top"),sQuery(id+"F8.wireOp",EDGE,"E362.right"),sQuery(id+"F8.wireOp",EDGE,"E363.right"),sQuery(id+"F8.wireOp",EDGE,"E364.bottom"),sQuery(id+"F8.wireOp",EDGE,"E365.right"),sQuery(id+"F8.wireOp",EDGE,"E366.right"),sQuery(id+"F8.wireOp",EDGE,"E367.bottom"),sQuery(id+"F8.wireOp",EDGE,"E368.right"),sQuery(id+"F8.wireOp",EDGE,"E369"),sQuery(id+"F8.wireOp",EDGE,"E370"),sQuery(id+"F8.wireOp",EDGE,"E371"),sQuery(id+"F8.wireOp",EDGE,"E372"),sQuery(id+"F8.wireOp",EDGE,"E373"),sQuery(id+"F8.wireOp",EDGE,"E374"),sQuery(id+"F8.wireOp",EDGE,"E375"),sQuery(id+"F8.wireOp",EDGE,"E376"),sQuery(id+"F8.wireOp",EDGE,"E378"),sQuery(id+"F8.wireOp",EDGE,"E379"),sQuery(id+"F8.wireOp",EDGE,"E380"),sQuery(id+"F8.wireOp",EDGE,"E381"),sQuery(id+"F8.wireOp",EDGE,"E382"),sQuery(id+"F8.wireOp",EDGE,"E383"),sQuery(id+"F8.wireOp",EDGE,"E384"),sQuery(id+"F8.wireOp",EDGE,"E385"),sQuery(id+"F8.wireOp",EDGE,"E386"),sQuery(id+"F8.wireOp",EDGE,"E387"),sQuery(id+"F8.wireOp",EDGE,"E388"),sQuery(id+"F8.wireOp",EDGE,"E389"),sQuery(id+"F8.wireOp",EDGE,"E390"),sQuery(id+"F8.wireOp",EDGE,"E391"),sQuery(id+"F8.wireOp",EDGE,"E392"),sQuery(id+"F8.wireOp",EDGE,"E393"),sQuery(id+"F8.wireOp",EDGE,"E394"),sQuery(id+"F8.wireOp",EDGE,"E395"),sQuery(id+"F8.wireOp",EDGE,"E396"),sQuery(id+"F8.wireOp",EDGE,"E397"),sQuery(id+"F8.wireOp",EDGE,"E398"),sQuery(id+"F8.wireOp",EDGE,"E399"),sQuery(id+"F8.wireOp",EDGE,"E400"),sQuery(id+"F8.wireOp",EDGE,"E401"),sQuery(id+"F8.wireOp",EDGE,"E402"),sQuery(id+"F8.wireOp",EDGE,"E403"),sQuery(id+"F8.wireOp",EDGE,"E404"),sQuery(id+"F8.wireOp",EDGE,"E406"),sQuery(id+"F8.wireOp",EDGE,"E407"),sQuery(id+"F8.wireOp",EDGE,"E408"),sQuery(id+"F8.wireOp",EDGE,"E409"),sQuery(id+"F8.wireOp",EDGE,"E410"),sQuery(id+"F8.wireOp",EDGE,"E411"),sQuery(id+"F8.wireOp",EDGE,"E412"),sQuery(id+"F8.wireOp",EDGE,"E413"),sQuery(id+"F8.wireOp",EDGE,"E414"),sQuery(id+"F8.wireOp",EDGE,"E415"),sQuery(id+"F8.wireOp",EDGE,"E416"),sQuery(id+"F8.wireOp",EDGE,"E417"),sQuery(id+"F8.wireOp",EDGE,"E418"),sQuery(id+"F8.wireOp",EDGE,"E419"),sQuery(id+"F8.wireOp",EDGE,"E420"),sQuery(id+"F8.wireOp",EDGE,"E421"),sQuery(id+"F8.wireOp",EDGE,"E422"),sQuery(id+"F8.wireOp",EDGE,"E423"),sQuery(id+"F8.wireOp",EDGE,"E424"),sQuery(id+"F8.wireOp",EDGE,"E425"),sQuery(id+"F8.wireOp",EDGE,"E426"),sQuery(id+"F8.wireOp",EDGE,"E427"),sQuery(id+"F8.wireOp",EDGE,"E428"),sQuery(id+"F8.wireOp",EDGE,"E429"),sQuery(id+"F8.wireOp",EDGE,"E430"),sQuery(id+"F8.wireOp",EDGE,"E431"),sQuery(id+"F8.wireOp",EDGE,"E432"),sQuery(id+"F8.wireOp",EDGE,"E433"),sQuery(id+"F8.wireOp",EDGE,"E434"),sQuery(id+"F8.wireOp",EDGE,"E435"),sQuery(id+"F8.wireOp",EDGE,"E436"),sQuery(id+"F8.wireOp",EDGE,"E437"),sQuery(id+"F8.wireOp",EDGE,"E438"),sQuery(id+"F8.wireOp",EDGE,"E439"),sQuery(id+"F8.wireOp",EDGE,"E440"),sQuery(id+"F8.wireOp",EDGE,"E441"),sQuery(id+"F8.wireOp",EDGE,"E442"),sQuery(id+"F8.wireOp",EDGE,"E443"),sQuery(id+"F8.wireOp",EDGE,"E444"),sQuery(id+"F8.wireOp",EDGE,"E445"),sQuery(id+"F8.wireOp",EDGE,"E446"),sQuery(id+"F8.wireOp",EDGE,"E447"),sQuery(id+"F8.wireOp",EDGE,"E448"),sQuery(id+"F8.wireOp",EDGE,"E449"),sQuery(id+"F8.wireOp",EDGE,"E450"),sQuery(id+"F8.wireOp",EDGE,"E451"),sQuery(id+"F8.wireOp",EDGE,"E452"),sQuery(id+"F8.wireOp",EDGE,"E453"),sQuery(id+"F8.wireOp",EDGE,"E454"),sQuery(id+"F8.wireOp",EDGE,"E455"),sQuery(id+"F8.wireOp",EDGE,"E456"),sQuery(id+"F8.wireOp",EDGE,"E457"),sQuery(id+"F8.wireOp",EDGE,"E458"),sQuery(id+"F8.wireOp",EDGE,"E459"),sQuery(id+"F8.wireOp",EDGE,"E460"),sQuery(id+"F8.wireOp",EDGE,"E461"),sQuery(id+"F8.wireOp",EDGE,"E462"),sQuery(id+"F8.wireOp",EDGE,"E463"),sQuery(id+"F8.wireOp",EDGE,"E464"),sQuery(id+"F8.wireOp",EDGE,"E465"),sQuery(id+"F8.wireOp",EDGE,"E466"),sQuery(id+"F8.wireOp",EDGE,"E467"),sQuery(id+"F8.wireOp",EDGE,"E468"),sQuery(id+"F8.wireOp",EDGE,"E469"),sQuery(id+"F8.wireOp",EDGE,"E470"),sQuery(id+"F8.wireOp",EDGE,"E471"),sQuery(id+"F8.wireOp",EDGE,"E472"),sQuery(id+"F8.wireOp",EDGE,"E473"),sQuery(id+"F8.wireOp",EDGE,"E474"),sQuery(id+"F8.wireOp",EDGE,"E475"),sQuery(id+"F8.wireOp",EDGE,"E476"),sQuery(id+"F8.wireOp",EDGE,"E477"),sQuery(id+"F8.wireOp",EDGE,"E478"),sQuery(id+"F8.wireOp",EDGE,"E479"),sQuery(id+"F8.wireOp",EDGE,"E480"),sQuery(id+"F8.wireOp",EDGE,"E481"),sQuery(id+"F8.wireOp",EDGE,"E482"),sQuery(id+"F8.wireOp",EDGE,"E483"),sQuery(id+"F8.wireOp",EDGE,"E484"),sQuery(id+"F8.wireOp",EDGE,"E485"),sQuery(id+"F8.wireOp",EDGE,"E486"),sQuery(id+"F8.wireOp",EDGE,"E487"),sQuery(id+"F8.wireOp",EDGE,"E488"),sQuery(id+"F8.wireOp",EDGE,"E489"),sQuery(id+"F8.wireOp",EDGE,"E490"),sQuery(id+"F8.wireOp",EDGE,"E491"),sQuery(id+"F8.wireOp",EDGE,"E492"),sQuery(id+"F8.wireOp",EDGE,"E493"),sQuery(id+"F8.wireOp",EDGE,"E494"),sQuery(id+"F8.wireOp",EDGE,"E495"),sQuery(id+"F8.wireOp",EDGE,"E496"),sQuery(id+"F8.wireOp",EDGE,"E497"),sQuery(id+"F8.wireOp",EDGE,"E498"),sQuery(id+"F8.wireOp",EDGE,"E499"),sQuery(id+"F8.wireOp",EDGE,"E500"),sQuery(id+"F8.wireOp",EDGE,"E501"),sQuery(id+"F8.wireOp",EDGE,"E502"),sQuery(id+"F8.wireOp",EDGE,"E503"),sQuery(id+"F8.wireOp",EDGE,"E504"),sQuery(id+"F8.wireOp",EDGE,"E505"),sQuery(id+"F8.wireOp",EDGE,"E506"),sQuery(id+"F8.wireOp",EDGE,"E507"),sQuery(id+"F8.wireOp",EDGE,"E508"),sQuery(id+"F8.wireOp",EDGE,"E510"),sQuery(id+"F8.wireOp",EDGE,"E511"),sQuery(id+"F8.wireOp",EDGE,"E512"),sQuery(id+"F8.wireOp",EDGE,"E513"),sQuery(id+"F8.wireOp",EDGE,"E514"),sQuery(id+"F8.wireOp",EDGE,"E515"),sQuery(id+"F8.wireOp",EDGE,"E516"),sQuery(id+"F8.wireOp",EDGE,"E517"),sQuery(id+"F8.wireOp",EDGE,"E518"),sQuery(id+"F8.wireOp",EDGE,"E519"),sQuery(id+"F8.wireOp",EDGE,"E520"),sQuery(id+"F8.wireOp",EDGE,"E521"),sQuery(id+"F8.wireOp",EDGE,"E522"),sQuery(id+"F8.wireOp",EDGE,"E523"),sQuery(id+"F8.wireOp",EDGE,"E524"),sQuery(id+"F8.wireOp",EDGE,"E525"),sQuery(id+"F8.wireOp",EDGE,"E526"),sQuery(id+"F8.wireOp",EDGE,"E527"),sQuery(id+"F8.wireOp",EDGE,"E528"),sQuery(id+"F8.wireOp",EDGE,"E529"),sQuery(id+"F8.wireOp",EDGE,"E530"),sQuery(id+"F8.wireOp",EDGE,"E531"),sQuery(id+"F8.wireOp",EDGE,"E532"),sQuery(id+"F8.wireOp",EDGE,"E533"),sQuery(id+"F8.wireOp",EDGE,"E534"),sQuery(id+"F8.wireOp",EDGE,"E535"),sQuery(id+"F8.wireOp",EDGE,"E536"),sQuery(id+"F8.wireOp",EDGE,"E537"),sQuery(id+"F8.wireOp",EDGE,"E538"),sQuery(id+"F8.wireOp",EDGE,"E539"),sQuery(id+"F8.wireOp",EDGE,"E540"),sQuery(id+"F8.wireOp",EDGE,"E541"),sQuery(id+"F8.wireOp",EDGE,"E542"),sQuery(id+"F8.wireOp",EDGE,"E543"),sQuery(id+"F8.wireOp",EDGE,"E544"),sQuery(id+"F8.wireOp",EDGE,"E545"),sQuery(id+"F8.wireOp",EDGE,"E546"),sQuery(id+"F8.wireOp",EDGE,"E547"),sQuery(id+"F8.wireOp",EDGE,"E548"),sQuery(id+"F8.wireOp",EDGE,"E549"),sQuery(id+"F8.wireOp",EDGE,"E550"),sQuery(id+"F8.wireOp",EDGE,"E551"),sQuery(id+"F8.wireOp",EDGE,"E552"),sQuery(id+"F8.wireOp",EDGE,"E553"),sQuery(id+"F8.wireOp",EDGE,"E554"),sQuery(id+"F8.wireOp",EDGE,"E555"),sQuery(id+"F8.wireOp",EDGE,"E556"),sQuery(id+"F8.wireOp",EDGE,"E557"),sQuery(id+"F8.wireOp",EDGE,"E558"),sQuery(id+"F8.wireOp",EDGE,"E559"),sQuery(id+"F8.wireOp",EDGE,"E560"),sQuery(id+"F8.wireOp",EDGE,"E561"),sQuery(id+"F8.wireOp",EDGE,"E562"),sQuery(id+"F8.wireOp",EDGE,"E563"),sQuery(id+"F8.wireOp",EDGE,"E564"),sQuery(id+"F8.wireOp",EDGE,"E565"),sQuery(id+"F8.wireOp",EDGE,"E566"),sQuery(id+"F8.wireOp",EDGE,"E567"),sQuery(id+"F8.wireOp",EDGE,"E568"),sQuery(id+"F8.wireOp",EDGE,"E569")])],"isStart":true});
            var sketch = newSketch(context, id + "F14", { "sketchPlane" : qUnion([Q0])});
            skLineSegment(sketch, "E840.bottom", {"start": v(-260.42, 402.85) * mm, "end": v(-50.87, 402.85) * mm});
            skLineSegment(sketch, "E840.top", {"start": v(-260.42, 421.9) * mm, "end": v(-50.87, 421.9) * mm});
            skLineSegment(sketch, "E841", {"start": v(-155.64, 402.85) * mm, "end": v(-155.64, 421.9) * mm});
            skLineSegment(sketch, "E842", {"start": v(-155.64, 415.55) * mm, "end": v(-158.82, 415.55) * mm});
            skLineSegment(sketch, "E843", {"start": v(-158.82, 415.55) * mm, "end": v(-158.82, 409.2) * mm});
            skLineSegment(sketch, "E844", {"start": v(-158.82, 409.2) * mm, "end": v(-155.64, 409.2) * mm});
            skLineSegment(sketch, "E845", {"start": v(-187.4, 409.2) * mm, "end": v(-184.22, 409.2) * mm});
            skLineSegment(sketch, "E846", {"start": v(-184.22, 409.2) * mm, "end": v(-184.22, 415.55) * mm});
            skLineSegment(sketch, "E847", {"start": v(-184.22, 415.55) * mm, "end": v(-187.4, 415.55) * mm});
            skLineSegment(sketch, "E848", {"start": v(-258.83, 409.2) * mm, "end": v(-258.83, 415.55) * mm});
            skLineSegment(sketch, "E849", {"start": v(-187.4, 409.2) * mm, "end": v(-187.4, 415.55) * mm});
            skLineSegment(sketch, "E850", {"start": v(-260.42, 402.85) * mm, "end": v(-260.42, 409.2) * mm});
            skLineSegment(sketch, "E851", {"start": v(-260.42, 409.2) * mm, "end": v(-258.83, 409.2) * mm});
            skLineSegment(sketch, "E852", {"start": v(-258.83, 415.55) * mm, "end": v(-260.42, 415.55) * mm});
            skLineSegment(sketch, "E853", {"start": v(-260.42, 415.55) * mm, "end": v(-260.42, 421.9) * mm});
            skLineSegment(sketch, "E854", {"start": v(-155.64, 409.2) * mm, "end": v(-152.47, 409.2) * mm});
            skLineSegment(sketch, "E855", {"start": v(-152.47, 409.2) * mm, "end": v(-152.47, 415.55) * mm});
            skLineSegment(sketch, "E856", {"start": v(-152.47, 415.55) * mm, "end": v(-155.64, 415.55) * mm});
            skLineSegment(sketch, "E857", {"start": v(-123.9, 415.55) * mm, "end": v(-127.07, 415.55) * mm});
            skLineSegment(sketch, "E858", {"start": v(-127.07, 415.55) * mm, "end": v(-127.07, 409.2) * mm});
            skLineSegment(sketch, "E859", {"start": v(-127.07, 409.2) * mm, "end": v(-123.9, 409.2) * mm});
            skLineSegment(sketch, "E860", {"start": v(-52.45, 415.55) * mm, "end": v(-52.45, 409.2) * mm});
            skLineSegment(sketch, "E861", {"start": v(-123.9, 415.55) * mm, "end": v(-123.9, 409.2) * mm});
            skLineSegment(sketch, "E862", {"start": v(-50.87, 402.85) * mm, "end": v(-50.87, 409.2) * mm});
            skLineSegment(sketch, "E863", {"start": v(-50.87, 409.2) * mm, "end": v(-52.45, 409.2) * mm});
            skLineSegment(sketch, "E864", {"start": v(-52.45, 415.55) * mm, "end": v(-50.87, 415.55) * mm});
            skLineSegment(sketch, "E865", {"start": v(-50.87, 415.55) * mm, "end": v(-50.87, 421.9) * mm});
            skSolve(sketch);
        }
        {
            var Q0;
            Q0 = qSketchRegion(id + "F14", true);
            extrude(context, id + "F15", {"entities" : qUnion([Q0]), "depth" : 3.17 * mm, "offsetDistance" : 25.4 * mm});
        }
    });
